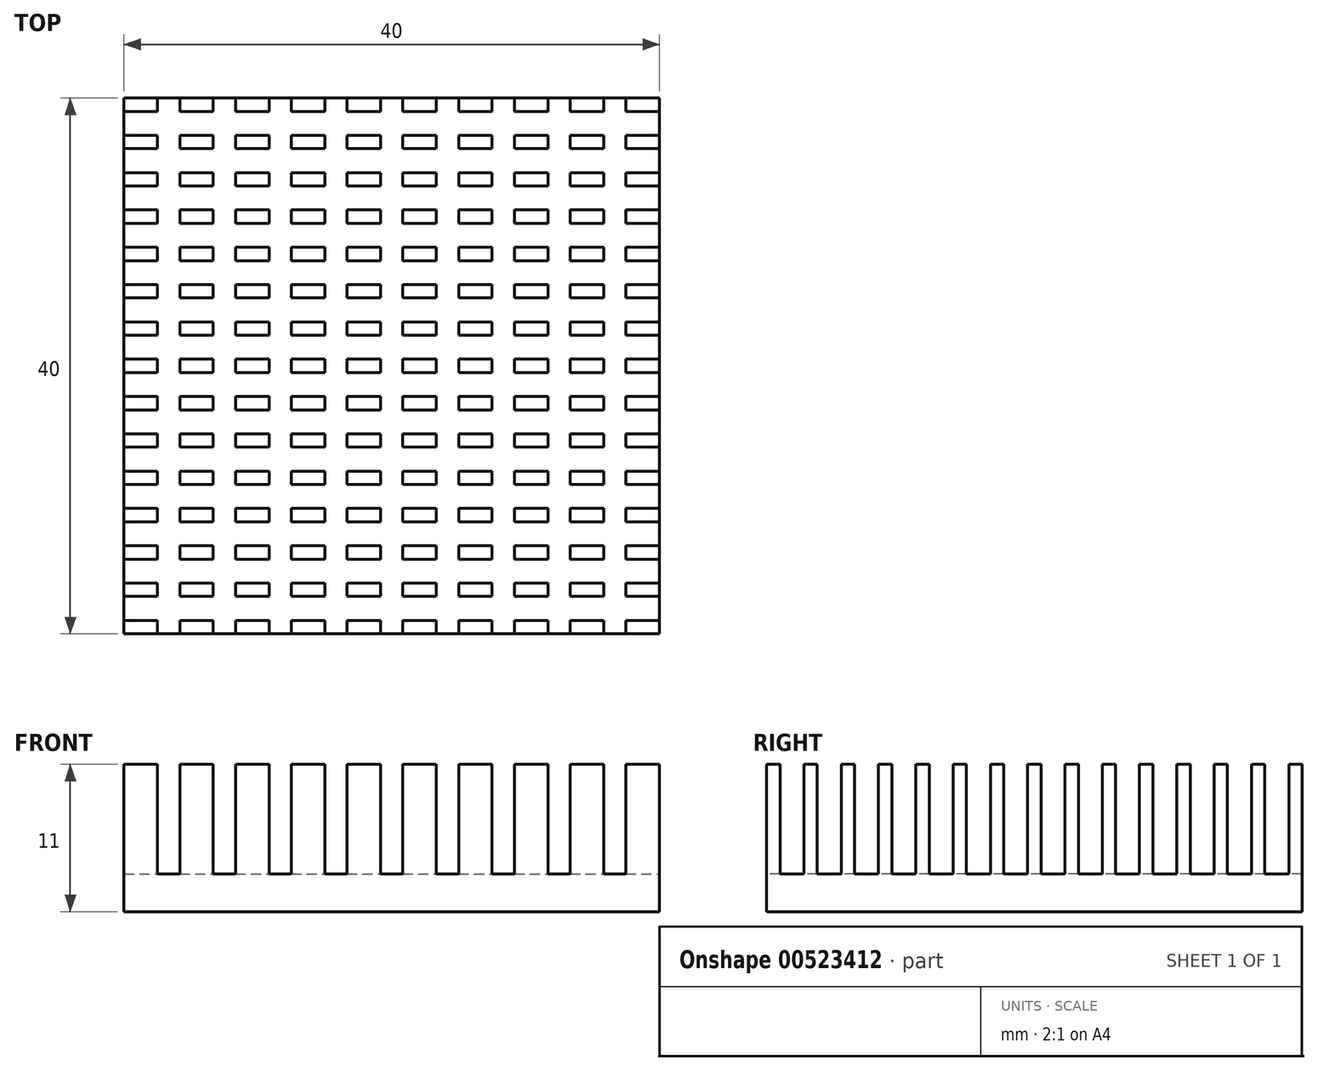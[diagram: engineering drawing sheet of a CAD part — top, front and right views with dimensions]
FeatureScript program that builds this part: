
annotation { "Feature Type Name" : "Feature", "Feature Type Description" : "" }
export const myFeature = defineFeature(function(context is Context, id is Id, definition is map)
    precondition{}
    {
        {
            var Q0;
            Q0=qCreatedBy(makeId("Top.planeOp"),FACE);
            var sketch = newSketch(context, id + "F0", { "sketchPlane" : qUnion([Q0])});
            skLineSegment(sketch, "E0.bottom", {"start": v(-20, 20) * mm, "end": v(20, 20) * mm});
            skLineSegment(sketch, "E0.top", {"start": v(-20, -20) * mm, "end": v(20, -20) * mm});
            skLineSegment(sketch, "E0.left", {"start": v(-20, 20) * mm, "end": v(-20, -20) * mm});
            skLineSegment(sketch, "E0.right", {"start": v(20, 20) * mm, "end": v(20, -20) * mm});
            skPoint(sketch, "E0.middle", {"position": v(0, 0) * mm});
            skSolve(sketch);
        }
        {
            var Q0;
            Q0 = qSketchRegion(id + "F0", true);
            extrude(context, id + "F1", {"entities" : qUnion([Q0]), "depth" : 2.8 * mm, "offsetDistance" : 25 * mm});
        }
        {
            var Q0;
            Q0=makeQuery(id+"F1.opExtrude","CAP_FACE",FACE,{"disambiguationData":[OSD([sQuery(id+"F0.wireOp",EDGE,"E0.bottom"),sQuery(id+"F0.wireOp",EDGE,"E0.top"),sQuery(id+"F0.wireOp",EDGE,"E0.left"),sQuery(id+"F0.wireOp",EDGE,"E0.right")])],"isStart":false});
            var sketch = newSketch(context, id + "F2", { "sketchPlane" : qUnion([Q0])});
            skLineSegment(sketch, "E1.bottom", {"start": v(-20, 20) * mm, "end": v(-17.5, 20) * mm});
            skLineSegment(sketch, "E1.top", {"start": v(-20, 19) * mm, "end": v(-17.5, 19) * mm});
            skLineSegment(sketch, "E1.left", {"start": v(-20, 20) * mm, "end": v(-20, 19) * mm});
            skLineSegment(sketch, "E1.right", {"start": v(-17.5, 20) * mm, "end": v(-17.5, 19) * mm});
            skPoint(sketch, "E1.middle", {"position": v(-18.75, 19.5) * mm});
            skLineSegment(sketch, "E2.1.0.0", {"start": v(-13.33, 20) * mm, "end": v(-13.33, 19) * mm});
            skLineSegment(sketch, "E2.1.0.1", {"start": v(-15.83, 20) * mm, "end": v(-15.83, 19) * mm});
            skLineSegment(sketch, "E2.1.0.2", {"start": v(-15.83, 19) * mm, "end": v(-13.33, 19) * mm});
            skLineSegment(sketch, "E2.1.0.3", {"start": v(-15.83, 20) * mm, "end": v(-13.33, 20) * mm});
            skPoint(sketch, "E2.1.0.4", {"position": v(-14.58, 19.5) * mm});
            skLineSegment(sketch, "E2.2.0.0", {"start": v(-9.17, 20) * mm, "end": v(-9.17, 19) * mm});
            skLineSegment(sketch, "E2.2.0.1", {"start": v(-11.67, 20) * mm, "end": v(-11.67, 19) * mm});
            skLineSegment(sketch, "E2.2.0.2", {"start": v(-11.67, 19) * mm, "end": v(-9.17, 19) * mm});
            skLineSegment(sketch, "E2.2.0.3", {"start": v(-11.67, 20) * mm, "end": v(-9.17, 20) * mm});
            skPoint(sketch, "E2.2.0.4", {"position": v(-10.42, 19.5) * mm});
            skLineSegment(sketch, "E2.3.0.0", {"start": v(-5, 20) * mm, "end": v(-5, 19) * mm});
            skLineSegment(sketch, "E2.3.0.1", {"start": v(-7.5, 20) * mm, "end": v(-7.5, 19) * mm});
            skLineSegment(sketch, "E2.3.0.2", {"start": v(-7.5, 19) * mm, "end": v(-5, 19) * mm});
            skLineSegment(sketch, "E2.3.0.3", {"start": v(-7.5, 20) * mm, "end": v(-5, 20) * mm});
            skPoint(sketch, "E2.3.0.4", {"position": v(-6.25, 19.5) * mm});
            skLineSegment(sketch, "E2.4.0.0", {"start": v(-0.83, 20) * mm, "end": v(-0.83, 19) * mm});
            skLineSegment(sketch, "E2.4.0.1", {"start": v(-3.33, 20) * mm, "end": v(-3.33, 19) * mm});
            skLineSegment(sketch, "E2.4.0.2", {"start": v(-3.33, 19) * mm, "end": v(-0.83, 19) * mm});
            skLineSegment(sketch, "E2.4.0.3", {"start": v(-3.33, 20) * mm, "end": v(-0.83, 20) * mm});
            skPoint(sketch, "E2.4.0.4", {"position": v(-2.08, 19.5) * mm});
            skLineSegment(sketch, "E2.5.0.0", {"start": v(3.33, 20) * mm, "end": v(3.33, 19) * mm});
            skLineSegment(sketch, "E2.5.0.1", {"start": v(0.83, 20) * mm, "end": v(0.83, 19) * mm});
            skLineSegment(sketch, "E2.5.0.2", {"start": v(0.83, 19) * mm, "end": v(3.33, 19) * mm});
            skLineSegment(sketch, "E2.5.0.3", {"start": v(0.83, 20) * mm, "end": v(3.33, 20) * mm});
            skPoint(sketch, "E2.5.0.4", {"position": v(2.08, 19.5) * mm});
            skLineSegment(sketch, "E2.6.0.0", {"start": v(7.5, 20) * mm, "end": v(7.5, 19) * mm});
            skLineSegment(sketch, "E2.6.0.1", {"start": v(5, 20) * mm, "end": v(5, 19) * mm});
            skLineSegment(sketch, "E2.6.0.2", {"start": v(5, 19) * mm, "end": v(7.5, 19) * mm});
            skLineSegment(sketch, "E2.6.0.3", {"start": v(5, 20) * mm, "end": v(7.5, 20) * mm});
            skPoint(sketch, "E2.6.0.4", {"position": v(6.25, 19.5) * mm});
            skLineSegment(sketch, "E2.7.0.0", {"start": v(11.67, 20) * mm, "end": v(11.67, 19) * mm});
            skLineSegment(sketch, "E2.7.0.1", {"start": v(9.17, 20) * mm, "end": v(9.17, 19) * mm});
            skLineSegment(sketch, "E2.7.0.2", {"start": v(9.17, 19) * mm, "end": v(11.67, 19) * mm});
            skLineSegment(sketch, "E2.7.0.3", {"start": v(9.17, 20) * mm, "end": v(11.67, 20) * mm});
            skPoint(sketch, "E2.7.0.4", {"position": v(10.42, 19.5) * mm});
            skLineSegment(sketch, "E2.8.0.0", {"start": v(15.83, 20) * mm, "end": v(15.83, 19) * mm});
            skLineSegment(sketch, "E2.8.0.1", {"start": v(13.33, 20) * mm, "end": v(13.33, 19) * mm});
            skLineSegment(sketch, "E2.8.0.2", {"start": v(13.33, 19) * mm, "end": v(15.83, 19) * mm});
            skLineSegment(sketch, "E2.8.0.3", {"start": v(13.33, 20) * mm, "end": v(15.83, 20) * mm});
            skPoint(sketch, "E2.8.0.4", {"position": v(14.58, 19.5) * mm});
            skLineSegment(sketch, "E2.9.0.0", {"start": v(20, 20) * mm, "end": v(20, 19) * mm});
            skLineSegment(sketch, "E2.9.0.1", {"start": v(17.5, 20) * mm, "end": v(17.5, 19) * mm});
            skLineSegment(sketch, "E2.9.0.2", {"start": v(17.5, 19) * mm, "end": v(20, 19) * mm});
            skLineSegment(sketch, "E2.9.0.3", {"start": v(17.5, 20) * mm, "end": v(20, 20) * mm});
            skPoint(sketch, "E2.9.0.4", {"position": v(18.75, 19.5) * mm});
            skLineSegment(sketch, "E2.direction1", {"start": v(-20, 19) * mm, "end": v(-15.83, 19) * mm, "construction": true});
            skPoint(sketch, "E3.1.0.0", {"position": v(2.08, 16.71) * mm});
            skLineSegment(sketch, "E3.1.0.1", {"start": v(5, 17.21) * mm, "end": v(7.5, 17.21) * mm});
            skLineSegment(sketch, "E3.1.0.2", {"start": v(17.5, 17.21) * mm, "end": v(20, 17.21) * mm});
            skLineSegment(sketch, "E3.1.0.3", {"start": v(0.83, 17.21) * mm, "end": v(3.33, 17.21) * mm});
            skPoint(sketch, "E3.1.0.4", {"position": v(18.75, 16.71) * mm});
            skPoint(sketch, "E3.1.0.5", {"position": v(-6.25, 16.71) * mm});
            skLineSegment(sketch, "E3.1.0.6", {"start": v(-20, 16.21) * mm, "end": v(-15.83, 16.21) * mm, "construction": true});
            skLineSegment(sketch, "E3.1.0.7", {"start": v(9.17, 16.21) * mm, "end": v(11.67, 16.21) * mm});
            skPoint(sketch, "E3.1.0.8", {"position": v(6.25, 16.71) * mm});
            skPoint(sketch, "E3.1.0.9", {"position": v(-2.08, 16.71) * mm});
            skLineSegment(sketch, "E3.1.0.10", {"start": v(-7.5, 16.21) * mm, "end": v(-5, 16.21) * mm});
            skPoint(sketch, "E3.1.0.11", {"position": v(-18.75, 16.71) * mm});
            skLineSegment(sketch, "E3.1.0.12", {"start": v(-7.5, 17.21) * mm, "end": v(-5, 17.21) * mm});
            skLineSegment(sketch, "E3.1.0.13", {"start": v(-20, 17.21) * mm, "end": v(-17.5, 17.21) * mm});
            skLineSegment(sketch, "E3.1.0.14", {"start": v(-15.83, 16.21) * mm, "end": v(-13.33, 16.21) * mm});
            skLineSegment(sketch, "E3.1.0.15", {"start": v(-15.83, 17.21) * mm, "end": v(-13.33, 17.21) * mm});
            skLineSegment(sketch, "E3.1.0.16", {"start": v(-11.67, 16.21) * mm, "end": v(-9.17, 16.21) * mm});
            skLineSegment(sketch, "E3.1.0.17", {"start": v(-11.67, 17.21) * mm, "end": v(-9.17, 17.21) * mm});
            skLineSegment(sketch, "E3.1.0.18", {"start": v(9.17, 17.21) * mm, "end": v(11.67, 17.21) * mm});
            skLineSegment(sketch, "E3.1.0.19", {"start": v(17.5, 16.21) * mm, "end": v(20, 16.21) * mm});
            skLineSegment(sketch, "E3.1.0.20", {"start": v(0.83, 16.21) * mm, "end": v(3.33, 16.21) * mm});
            skLineSegment(sketch, "E3.1.0.21", {"start": v(13.33, 16.21) * mm, "end": v(15.83, 16.21) * mm});
            skLineSegment(sketch, "E3.1.0.22", {"start": v(-3.33, 16.21) * mm, "end": v(-0.83, 16.21) * mm});
            skPoint(sketch, "E3.1.0.23", {"position": v(10.42, 16.71) * mm});
            skPoint(sketch, "E3.1.0.24", {"position": v(-14.58, 16.71) * mm});
            skLineSegment(sketch, "E3.1.0.25", {"start": v(5, 16.21) * mm, "end": v(7.5, 16.21) * mm});
            skLineSegment(sketch, "E3.1.0.26", {"start": v(13.33, 17.21) * mm, "end": v(15.83, 17.21) * mm});
            skLineSegment(sketch, "E3.1.0.27", {"start": v(-3.33, 17.21) * mm, "end": v(-0.83, 17.21) * mm});
            skPoint(sketch, "E3.1.0.28", {"position": v(14.58, 16.71) * mm});
            skPoint(sketch, "E3.1.0.29", {"position": v(-10.42, 16.71) * mm});
            skLineSegment(sketch, "E3.1.0.30", {"start": v(-20, 16.21) * mm, "end": v(-17.5, 16.21) * mm});
            skLineSegment(sketch, "E3.1.0.31", {"start": v(20, 17.21) * mm, "end": v(20, 16.21) * mm});
            skLineSegment(sketch, "E3.1.0.32", {"start": v(9.17, 17.21) * mm, "end": v(9.17, 16.21) * mm});
            skLineSegment(sketch, "E3.1.0.33", {"start": v(3.33, 17.21) * mm, "end": v(3.33, 16.21) * mm});
            skLineSegment(sketch, "E3.1.0.34", {"start": v(15.83, 17.21) * mm, "end": v(15.83, 16.21) * mm});
            skLineSegment(sketch, "E3.1.0.35", {"start": v(-0.83, 17.21) * mm, "end": v(-0.83, 16.21) * mm});
            skLineSegment(sketch, "E3.1.0.36", {"start": v(11.67, 17.21) * mm, "end": v(11.67, 16.21) * mm});
            skLineSegment(sketch, "E3.1.0.37", {"start": v(7.5, 17.21) * mm, "end": v(7.5, 16.21) * mm});
            skLineSegment(sketch, "E3.1.0.38", {"start": v(17.5, 17.21) * mm, "end": v(17.5, 16.21) * mm});
            skLineSegment(sketch, "E3.1.0.39", {"start": v(0.83, 17.21) * mm, "end": v(0.83, 16.21) * mm});
            skLineSegment(sketch, "E3.1.0.40", {"start": v(13.33, 17.21) * mm, "end": v(13.33, 16.21) * mm});
            skLineSegment(sketch, "E3.1.0.41", {"start": v(-3.33, 17.21) * mm, "end": v(-3.33, 16.21) * mm});
            skLineSegment(sketch, "E3.1.0.42", {"start": v(-7.5, 17.21) * mm, "end": v(-7.5, 16.21) * mm});
            skLineSegment(sketch, "E3.1.0.43", {"start": v(-20, 17.21) * mm, "end": v(-20, 16.21) * mm});
            skLineSegment(sketch, "E3.1.0.44", {"start": v(-17.5, 17.21) * mm, "end": v(-17.5, 16.21) * mm});
            skLineSegment(sketch, "E3.1.0.45", {"start": v(-13.33, 17.21) * mm, "end": v(-13.33, 16.21) * mm});
            skLineSegment(sketch, "E3.1.0.46", {"start": v(-15.83, 17.21) * mm, "end": v(-15.83, 16.21) * mm});
            skLineSegment(sketch, "E3.1.0.47", {"start": v(-9.17, 17.21) * mm, "end": v(-9.17, 16.21) * mm});
            skLineSegment(sketch, "E3.1.0.48", {"start": v(-11.67, 17.21) * mm, "end": v(-11.67, 16.21) * mm});
            skLineSegment(sketch, "E3.1.0.49", {"start": v(5, 17.21) * mm, "end": v(5, 16.21) * mm});
            skLineSegment(sketch, "E3.1.0.50", {"start": v(-5, 17.21) * mm, "end": v(-5, 16.21) * mm});
            skPoint(sketch, "E3.2.0.0", {"position": v(2.08, 13.93) * mm});
            skLineSegment(sketch, "E3.2.0.1", {"start": v(5, 14.43) * mm, "end": v(7.5, 14.43) * mm});
            skLineSegment(sketch, "E3.2.0.2", {"start": v(17.5, 14.43) * mm, "end": v(20, 14.43) * mm});
            skLineSegment(sketch, "E3.2.0.3", {"start": v(0.83, 14.43) * mm, "end": v(3.33, 14.43) * mm});
            skPoint(sketch, "E3.2.0.4", {"position": v(18.75, 13.93) * mm});
            skPoint(sketch, "E3.2.0.5", {"position": v(-6.25, 13.93) * mm});
            skLineSegment(sketch, "E3.2.0.6", {"start": v(-20, 13.43) * mm, "end": v(-15.83, 13.43) * mm, "construction": true});
            skLineSegment(sketch, "E3.2.0.7", {"start": v(9.17, 13.43) * mm, "end": v(11.67, 13.43) * mm});
            skPoint(sketch, "E3.2.0.8", {"position": v(6.25, 13.93) * mm});
            skPoint(sketch, "E3.2.0.9", {"position": v(-2.08, 13.93) * mm});
            skLineSegment(sketch, "E3.2.0.10", {"start": v(-7.5, 13.43) * mm, "end": v(-5, 13.43) * mm});
            skPoint(sketch, "E3.2.0.11", {"position": v(-18.75, 13.93) * mm});
            skLineSegment(sketch, "E3.2.0.12", {"start": v(-7.5, 14.43) * mm, "end": v(-5, 14.43) * mm});
            skLineSegment(sketch, "E3.2.0.13", {"start": v(-20, 14.43) * mm, "end": v(-17.5, 14.43) * mm});
            skLineSegment(sketch, "E3.2.0.14", {"start": v(-15.83, 13.43) * mm, "end": v(-13.33, 13.43) * mm});
            skLineSegment(sketch, "E3.2.0.15", {"start": v(-15.83, 14.43) * mm, "end": v(-13.33, 14.43) * mm});
            skLineSegment(sketch, "E3.2.0.16", {"start": v(-11.67, 13.43) * mm, "end": v(-9.17, 13.43) * mm});
            skLineSegment(sketch, "E3.2.0.17", {"start": v(-11.67, 14.43) * mm, "end": v(-9.17, 14.43) * mm});
            skLineSegment(sketch, "E3.2.0.18", {"start": v(9.17, 14.43) * mm, "end": v(11.67, 14.43) * mm});
            skLineSegment(sketch, "E3.2.0.19", {"start": v(17.5, 13.43) * mm, "end": v(20, 13.43) * mm});
            skLineSegment(sketch, "E3.2.0.20", {"start": v(0.83, 13.43) * mm, "end": v(3.33, 13.43) * mm});
            skLineSegment(sketch, "E3.2.0.21", {"start": v(13.33, 13.43) * mm, "end": v(15.83, 13.43) * mm});
            skLineSegment(sketch, "E3.2.0.22", {"start": v(-3.33, 13.43) * mm, "end": v(-0.83, 13.43) * mm});
            skPoint(sketch, "E3.2.0.23", {"position": v(10.42, 13.93) * mm});
            skPoint(sketch, "E3.2.0.24", {"position": v(-14.58, 13.93) * mm});
            skLineSegment(sketch, "E3.2.0.25", {"start": v(5, 13.43) * mm, "end": v(7.5, 13.43) * mm});
            skLineSegment(sketch, "E3.2.0.26", {"start": v(13.33, 14.43) * mm, "end": v(15.83, 14.43) * mm});
            skLineSegment(sketch, "E3.2.0.27", {"start": v(-3.33, 14.43) * mm, "end": v(-0.83, 14.43) * mm});
            skPoint(sketch, "E3.2.0.28", {"position": v(14.58, 13.93) * mm});
            skPoint(sketch, "E3.2.0.29", {"position": v(-10.42, 13.93) * mm});
            skLineSegment(sketch, "E3.2.0.30", {"start": v(-20, 13.43) * mm, "end": v(-17.5, 13.43) * mm});
            skLineSegment(sketch, "E3.2.0.31", {"start": v(20, 14.43) * mm, "end": v(20, 13.43) * mm});
            skLineSegment(sketch, "E3.2.0.32", {"start": v(9.17, 14.43) * mm, "end": v(9.17, 13.43) * mm});
            skLineSegment(sketch, "E3.2.0.33", {"start": v(3.33, 14.43) * mm, "end": v(3.33, 13.43) * mm});
            skLineSegment(sketch, "E3.2.0.34", {"start": v(15.83, 14.43) * mm, "end": v(15.83, 13.43) * mm});
            skLineSegment(sketch, "E3.2.0.35", {"start": v(-0.83, 14.43) * mm, "end": v(-0.83, 13.43) * mm});
            skLineSegment(sketch, "E3.2.0.36", {"start": v(11.67, 14.43) * mm, "end": v(11.67, 13.43) * mm});
            skLineSegment(sketch, "E3.2.0.37", {"start": v(7.5, 14.43) * mm, "end": v(7.5, 13.43) * mm});
            skLineSegment(sketch, "E3.2.0.38", {"start": v(17.5, 14.43) * mm, "end": v(17.5, 13.43) * mm});
            skLineSegment(sketch, "E3.2.0.39", {"start": v(0.83, 14.43) * mm, "end": v(0.83, 13.43) * mm});
            skLineSegment(sketch, "E3.2.0.40", {"start": v(13.33, 14.43) * mm, "end": v(13.33, 13.43) * mm});
            skLineSegment(sketch, "E3.2.0.41", {"start": v(-3.33, 14.43) * mm, "end": v(-3.33, 13.43) * mm});
            skLineSegment(sketch, "E3.2.0.42", {"start": v(-7.5, 14.43) * mm, "end": v(-7.5, 13.43) * mm});
            skLineSegment(sketch, "E3.2.0.43", {"start": v(-20, 14.43) * mm, "end": v(-20, 13.43) * mm});
            skLineSegment(sketch, "E3.2.0.44", {"start": v(-17.5, 14.43) * mm, "end": v(-17.5, 13.43) * mm});
            skLineSegment(sketch, "E3.2.0.45", {"start": v(-13.33, 14.43) * mm, "end": v(-13.33, 13.43) * mm});
            skLineSegment(sketch, "E3.2.0.46", {"start": v(-15.83, 14.43) * mm, "end": v(-15.83, 13.43) * mm});
            skLineSegment(sketch, "E3.2.0.47", {"start": v(-9.17, 14.43) * mm, "end": v(-9.17, 13.43) * mm});
            skLineSegment(sketch, "E3.2.0.48", {"start": v(-11.67, 14.43) * mm, "end": v(-11.67, 13.43) * mm});
            skLineSegment(sketch, "E3.2.0.49", {"start": v(5, 14.43) * mm, "end": v(5, 13.43) * mm});
            skLineSegment(sketch, "E3.2.0.50", {"start": v(-5, 14.43) * mm, "end": v(-5, 13.43) * mm});
            skPoint(sketch, "E3.3.0.0", {"position": v(2.08, 11.14) * mm});
            skLineSegment(sketch, "E3.3.0.1", {"start": v(5, 11.64) * mm, "end": v(7.5, 11.64) * mm});
            skLineSegment(sketch, "E3.3.0.2", {"start": v(17.5, 11.64) * mm, "end": v(20, 11.64) * mm});
            skLineSegment(sketch, "E3.3.0.3", {"start": v(0.83, 11.64) * mm, "end": v(3.33, 11.64) * mm});
            skPoint(sketch, "E3.3.0.4", {"position": v(18.75, 11.14) * mm});
            skPoint(sketch, "E3.3.0.5", {"position": v(-6.25, 11.14) * mm});
            skLineSegment(sketch, "E3.3.0.6", {"start": v(-20, 10.64) * mm, "end": v(-15.83, 10.64) * mm, "construction": true});
            skLineSegment(sketch, "E3.3.0.7", {"start": v(9.17, 10.64) * mm, "end": v(11.67, 10.64) * mm});
            skPoint(sketch, "E3.3.0.8", {"position": v(6.25, 11.14) * mm});
            skPoint(sketch, "E3.3.0.9", {"position": v(-2.08, 11.14) * mm});
            skLineSegment(sketch, "E3.3.0.10", {"start": v(-7.5, 10.64) * mm, "end": v(-5, 10.64) * mm});
            skPoint(sketch, "E3.3.0.11", {"position": v(-18.75, 11.14) * mm});
            skLineSegment(sketch, "E3.3.0.12", {"start": v(-7.5, 11.64) * mm, "end": v(-5, 11.64) * mm});
            skLineSegment(sketch, "E3.3.0.13", {"start": v(-20, 11.64) * mm, "end": v(-17.5, 11.64) * mm});
            skLineSegment(sketch, "E3.3.0.14", {"start": v(-15.83, 10.64) * mm, "end": v(-13.33, 10.64) * mm});
            skLineSegment(sketch, "E3.3.0.15", {"start": v(-15.83, 11.64) * mm, "end": v(-13.33, 11.64) * mm});
            skLineSegment(sketch, "E3.3.0.16", {"start": v(-11.67, 10.64) * mm, "end": v(-9.17, 10.64) * mm});
            skLineSegment(sketch, "E3.3.0.17", {"start": v(-11.67, 11.64) * mm, "end": v(-9.17, 11.64) * mm});
            skLineSegment(sketch, "E3.3.0.18", {"start": v(9.17, 11.64) * mm, "end": v(11.67, 11.64) * mm});
            skLineSegment(sketch, "E3.3.0.19", {"start": v(17.5, 10.64) * mm, "end": v(20, 10.64) * mm});
            skLineSegment(sketch, "E3.3.0.20", {"start": v(0.83, 10.64) * mm, "end": v(3.33, 10.64) * mm});
            skLineSegment(sketch, "E3.3.0.21", {"start": v(13.33, 10.64) * mm, "end": v(15.83, 10.64) * mm});
            skLineSegment(sketch, "E3.3.0.22", {"start": v(-3.33, 10.64) * mm, "end": v(-0.83, 10.64) * mm});
            skPoint(sketch, "E3.3.0.23", {"position": v(10.42, 11.14) * mm});
            skPoint(sketch, "E3.3.0.24", {"position": v(-14.58, 11.14) * mm});
            skLineSegment(sketch, "E3.3.0.25", {"start": v(5, 10.64) * mm, "end": v(7.5, 10.64) * mm});
            skLineSegment(sketch, "E3.3.0.26", {"start": v(13.33, 11.64) * mm, "end": v(15.83, 11.64) * mm});
            skLineSegment(sketch, "E3.3.0.27", {"start": v(-3.33, 11.64) * mm, "end": v(-0.83, 11.64) * mm});
            skPoint(sketch, "E3.3.0.28", {"position": v(14.58, 11.14) * mm});
            skPoint(sketch, "E3.3.0.29", {"position": v(-10.42, 11.14) * mm});
            skLineSegment(sketch, "E3.3.0.30", {"start": v(-20, 10.64) * mm, "end": v(-17.5, 10.64) * mm});
            skLineSegment(sketch, "E3.3.0.31", {"start": v(20, 11.64) * mm, "end": v(20, 10.64) * mm});
            skLineSegment(sketch, "E3.3.0.32", {"start": v(9.17, 11.64) * mm, "end": v(9.17, 10.64) * mm});
            skLineSegment(sketch, "E3.3.0.33", {"start": v(3.33, 11.64) * mm, "end": v(3.33, 10.64) * mm});
            skLineSegment(sketch, "E3.3.0.34", {"start": v(15.83, 11.64) * mm, "end": v(15.83, 10.64) * mm});
            skLineSegment(sketch, "E3.3.0.35", {"start": v(-0.83, 11.64) * mm, "end": v(-0.83, 10.64) * mm});
            skLineSegment(sketch, "E3.3.0.36", {"start": v(11.67, 11.64) * mm, "end": v(11.67, 10.64) * mm});
            skLineSegment(sketch, "E3.3.0.37", {"start": v(7.5, 11.64) * mm, "end": v(7.5, 10.64) * mm});
            skLineSegment(sketch, "E3.3.0.38", {"start": v(17.5, 11.64) * mm, "end": v(17.5, 10.64) * mm});
            skLineSegment(sketch, "E3.3.0.39", {"start": v(0.83, 11.64) * mm, "end": v(0.83, 10.64) * mm});
            skLineSegment(sketch, "E3.3.0.40", {"start": v(13.33, 11.64) * mm, "end": v(13.33, 10.64) * mm});
            skLineSegment(sketch, "E3.3.0.41", {"start": v(-3.33, 11.64) * mm, "end": v(-3.33, 10.64) * mm});
            skLineSegment(sketch, "E3.3.0.42", {"start": v(-7.5, 11.64) * mm, "end": v(-7.5, 10.64) * mm});
            skLineSegment(sketch, "E3.3.0.43", {"start": v(-20, 11.64) * mm, "end": v(-20, 10.64) * mm});
            skLineSegment(sketch, "E3.3.0.44", {"start": v(-17.5, 11.64) * mm, "end": v(-17.5, 10.64) * mm});
            skLineSegment(sketch, "E3.3.0.45", {"start": v(-13.33, 11.64) * mm, "end": v(-13.33, 10.64) * mm});
            skLineSegment(sketch, "E3.3.0.46", {"start": v(-15.83, 11.64) * mm, "end": v(-15.83, 10.64) * mm});
            skLineSegment(sketch, "E3.3.0.47", {"start": v(-9.17, 11.64) * mm, "end": v(-9.17, 10.64) * mm});
            skLineSegment(sketch, "E3.3.0.48", {"start": v(-11.67, 11.64) * mm, "end": v(-11.67, 10.64) * mm});
            skLineSegment(sketch, "E3.3.0.49", {"start": v(5, 11.64) * mm, "end": v(5, 10.64) * mm});
            skLineSegment(sketch, "E3.3.0.50", {"start": v(-5, 11.64) * mm, "end": v(-5, 10.64) * mm});
            skPoint(sketch, "E3.4.0.0", {"position": v(2.08, 8.36) * mm});
            skLineSegment(sketch, "E3.4.0.1", {"start": v(5, 8.86) * mm, "end": v(7.5, 8.86) * mm});
            skLineSegment(sketch, "E3.4.0.2", {"start": v(17.5, 8.86) * mm, "end": v(20, 8.86) * mm});
            skLineSegment(sketch, "E3.4.0.3", {"start": v(0.83, 8.86) * mm, "end": v(3.33, 8.86) * mm});
            skPoint(sketch, "E3.4.0.4", {"position": v(18.75, 8.36) * mm});
            skPoint(sketch, "E3.4.0.5", {"position": v(-6.25, 8.36) * mm});
            skLineSegment(sketch, "E3.4.0.6", {"start": v(-20, 7.86) * mm, "end": v(-15.83, 7.86) * mm, "construction": true});
            skLineSegment(sketch, "E3.4.0.7", {"start": v(9.17, 7.86) * mm, "end": v(11.67, 7.86) * mm});
            skPoint(sketch, "E3.4.0.8", {"position": v(6.25, 8.36) * mm});
            skPoint(sketch, "E3.4.0.9", {"position": v(-2.08, 8.36) * mm});
            skLineSegment(sketch, "E3.4.0.10", {"start": v(-7.5, 7.86) * mm, "end": v(-5, 7.86) * mm});
            skPoint(sketch, "E3.4.0.11", {"position": v(-18.75, 8.36) * mm});
            skLineSegment(sketch, "E3.4.0.12", {"start": v(-7.5, 8.86) * mm, "end": v(-5, 8.86) * mm});
            skLineSegment(sketch, "E3.4.0.13", {"start": v(-20, 8.86) * mm, "end": v(-17.5, 8.86) * mm});
            skLineSegment(sketch, "E3.4.0.14", {"start": v(-15.83, 7.86) * mm, "end": v(-13.33, 7.86) * mm});
            skLineSegment(sketch, "E3.4.0.15", {"start": v(-15.83, 8.86) * mm, "end": v(-13.33, 8.86) * mm});
            skLineSegment(sketch, "E3.4.0.16", {"start": v(-11.67, 7.86) * mm, "end": v(-9.17, 7.86) * mm});
            skLineSegment(sketch, "E3.4.0.17", {"start": v(-11.67, 8.86) * mm, "end": v(-9.17, 8.86) * mm});
            skLineSegment(sketch, "E3.4.0.18", {"start": v(9.17, 8.86) * mm, "end": v(11.67, 8.86) * mm});
            skLineSegment(sketch, "E3.4.0.19", {"start": v(17.5, 7.86) * mm, "end": v(20, 7.86) * mm});
            skLineSegment(sketch, "E3.4.0.20", {"start": v(0.83, 7.86) * mm, "end": v(3.33, 7.86) * mm});
            skLineSegment(sketch, "E3.4.0.21", {"start": v(13.33, 7.86) * mm, "end": v(15.83, 7.86) * mm});
            skLineSegment(sketch, "E3.4.0.22", {"start": v(-3.33, 7.86) * mm, "end": v(-0.83, 7.86) * mm});
            skPoint(sketch, "E3.4.0.23", {"position": v(10.42, 8.36) * mm});
            skPoint(sketch, "E3.4.0.24", {"position": v(-14.58, 8.36) * mm});
            skLineSegment(sketch, "E3.4.0.25", {"start": v(5, 7.86) * mm, "end": v(7.5, 7.86) * mm});
            skLineSegment(sketch, "E3.4.0.26", {"start": v(13.33, 8.86) * mm, "end": v(15.83, 8.86) * mm});
            skLineSegment(sketch, "E3.4.0.27", {"start": v(-3.33, 8.86) * mm, "end": v(-0.83, 8.86) * mm});
            skPoint(sketch, "E3.4.0.28", {"position": v(14.58, 8.36) * mm});
            skPoint(sketch, "E3.4.0.29", {"position": v(-10.42, 8.36) * mm});
            skLineSegment(sketch, "E3.4.0.30", {"start": v(-20, 7.86) * mm, "end": v(-17.5, 7.86) * mm});
            skLineSegment(sketch, "E3.4.0.31", {"start": v(20, 8.86) * mm, "end": v(20, 7.86) * mm});
            skLineSegment(sketch, "E3.4.0.32", {"start": v(9.17, 8.86) * mm, "end": v(9.17, 7.86) * mm});
            skLineSegment(sketch, "E3.4.0.33", {"start": v(3.33, 8.86) * mm, "end": v(3.33, 7.86) * mm});
            skLineSegment(sketch, "E3.4.0.34", {"start": v(15.83, 8.86) * mm, "end": v(15.83, 7.86) * mm});
            skLineSegment(sketch, "E3.4.0.35", {"start": v(-0.83, 8.86) * mm, "end": v(-0.83, 7.86) * mm});
            skLineSegment(sketch, "E3.4.0.36", {"start": v(11.67, 8.86) * mm, "end": v(11.67, 7.86) * mm});
            skLineSegment(sketch, "E3.4.0.37", {"start": v(7.5, 8.86) * mm, "end": v(7.5, 7.86) * mm});
            skLineSegment(sketch, "E3.4.0.38", {"start": v(17.5, 8.86) * mm, "end": v(17.5, 7.86) * mm});
            skLineSegment(sketch, "E3.4.0.39", {"start": v(0.83, 8.86) * mm, "end": v(0.83, 7.86) * mm});
            skLineSegment(sketch, "E3.4.0.40", {"start": v(13.33, 8.86) * mm, "end": v(13.33, 7.86) * mm});
            skLineSegment(sketch, "E3.4.0.41", {"start": v(-3.33, 8.86) * mm, "end": v(-3.33, 7.86) * mm});
            skLineSegment(sketch, "E3.4.0.42", {"start": v(-7.5, 8.86) * mm, "end": v(-7.5, 7.86) * mm});
            skLineSegment(sketch, "E3.4.0.43", {"start": v(-20, 8.86) * mm, "end": v(-20, 7.86) * mm});
            skLineSegment(sketch, "E3.4.0.44", {"start": v(-17.5, 8.86) * mm, "end": v(-17.5, 7.86) * mm});
            skLineSegment(sketch, "E3.4.0.45", {"start": v(-13.33, 8.86) * mm, "end": v(-13.33, 7.86) * mm});
            skLineSegment(sketch, "E3.4.0.46", {"start": v(-15.83, 8.86) * mm, "end": v(-15.83, 7.86) * mm});
            skLineSegment(sketch, "E3.4.0.47", {"start": v(-9.17, 8.86) * mm, "end": v(-9.17, 7.86) * mm});
            skLineSegment(sketch, "E3.4.0.48", {"start": v(-11.67, 8.86) * mm, "end": v(-11.67, 7.86) * mm});
            skLineSegment(sketch, "E3.4.0.49", {"start": v(5, 8.86) * mm, "end": v(5, 7.86) * mm});
            skLineSegment(sketch, "E3.4.0.50", {"start": v(-5, 8.86) * mm, "end": v(-5, 7.86) * mm});
            skPoint(sketch, "E3.5.0.0", {"position": v(2.08, 5.57) * mm});
            skLineSegment(sketch, "E3.5.0.1", {"start": v(5, 6.07) * mm, "end": v(7.5, 6.07) * mm});
            skLineSegment(sketch, "E3.5.0.2", {"start": v(17.5, 6.07) * mm, "end": v(20, 6.07) * mm});
            skLineSegment(sketch, "E3.5.0.3", {"start": v(0.83, 6.07) * mm, "end": v(3.33, 6.07) * mm});
            skPoint(sketch, "E3.5.0.4", {"position": v(18.75, 5.57) * mm});
            skPoint(sketch, "E3.5.0.5", {"position": v(-6.25, 5.57) * mm});
            skLineSegment(sketch, "E3.5.0.6", {"start": v(-20, 5.07) * mm, "end": v(-15.83, 5.07) * mm, "construction": true});
            skLineSegment(sketch, "E3.5.0.7", {"start": v(9.17, 5.07) * mm, "end": v(11.67, 5.07) * mm});
            skPoint(sketch, "E3.5.0.8", {"position": v(6.25, 5.57) * mm});
            skPoint(sketch, "E3.5.0.9", {"position": v(-2.08, 5.57) * mm});
            skLineSegment(sketch, "E3.5.0.10", {"start": v(-7.5, 5.07) * mm, "end": v(-5, 5.07) * mm});
            skPoint(sketch, "E3.5.0.11", {"position": v(-18.75, 5.57) * mm});
            skLineSegment(sketch, "E3.5.0.12", {"start": v(-7.5, 6.07) * mm, "end": v(-5, 6.07) * mm});
            skLineSegment(sketch, "E3.5.0.13", {"start": v(-20, 6.07) * mm, "end": v(-17.5, 6.07) * mm});
            skLineSegment(sketch, "E3.5.0.14", {"start": v(-15.83, 5.07) * mm, "end": v(-13.33, 5.07) * mm});
            skLineSegment(sketch, "E3.5.0.15", {"start": v(-15.83, 6.07) * mm, "end": v(-13.33, 6.07) * mm});
            skLineSegment(sketch, "E3.5.0.16", {"start": v(-11.67, 5.07) * mm, "end": v(-9.17, 5.07) * mm});
            skLineSegment(sketch, "E3.5.0.17", {"start": v(-11.67, 6.07) * mm, "end": v(-9.17, 6.07) * mm});
            skLineSegment(sketch, "E3.5.0.18", {"start": v(9.17, 6.07) * mm, "end": v(11.67, 6.07) * mm});
            skLineSegment(sketch, "E3.5.0.19", {"start": v(17.5, 5.07) * mm, "end": v(20, 5.07) * mm});
            skLineSegment(sketch, "E3.5.0.20", {"start": v(0.83, 5.07) * mm, "end": v(3.33, 5.07) * mm});
            skLineSegment(sketch, "E3.5.0.21", {"start": v(13.33, 5.07) * mm, "end": v(15.83, 5.07) * mm});
            skLineSegment(sketch, "E3.5.0.22", {"start": v(-3.33, 5.07) * mm, "end": v(-0.83, 5.07) * mm});
            skPoint(sketch, "E3.5.0.23", {"position": v(10.42, 5.57) * mm});
            skPoint(sketch, "E3.5.0.24", {"position": v(-14.58, 5.57) * mm});
            skLineSegment(sketch, "E3.5.0.25", {"start": v(5, 5.07) * mm, "end": v(7.5, 5.07) * mm});
            skLineSegment(sketch, "E3.5.0.26", {"start": v(13.33, 6.07) * mm, "end": v(15.83, 6.07) * mm});
            skLineSegment(sketch, "E3.5.0.27", {"start": v(-3.33, 6.07) * mm, "end": v(-0.83, 6.07) * mm});
            skPoint(sketch, "E3.5.0.28", {"position": v(14.58, 5.57) * mm});
            skPoint(sketch, "E3.5.0.29", {"position": v(-10.42, 5.57) * mm});
            skLineSegment(sketch, "E3.5.0.30", {"start": v(-20, 5.07) * mm, "end": v(-17.5, 5.07) * mm});
            skLineSegment(sketch, "E3.5.0.31", {"start": v(20, 6.07) * mm, "end": v(20, 5.07) * mm});
            skLineSegment(sketch, "E3.5.0.32", {"start": v(9.17, 6.07) * mm, "end": v(9.17, 5.07) * mm});
            skLineSegment(sketch, "E3.5.0.33", {"start": v(3.33, 6.07) * mm, "end": v(3.33, 5.07) * mm});
            skLineSegment(sketch, "E3.5.0.34", {"start": v(15.83, 6.07) * mm, "end": v(15.83, 5.07) * mm});
            skLineSegment(sketch, "E3.5.0.35", {"start": v(-0.83, 6.07) * mm, "end": v(-0.83, 5.07) * mm});
            skLineSegment(sketch, "E3.5.0.36", {"start": v(11.67, 6.07) * mm, "end": v(11.67, 5.07) * mm});
            skLineSegment(sketch, "E3.5.0.37", {"start": v(7.5, 6.07) * mm, "end": v(7.5, 5.07) * mm});
            skLineSegment(sketch, "E3.5.0.38", {"start": v(17.5, 6.07) * mm, "end": v(17.5, 5.07) * mm});
            skLineSegment(sketch, "E3.5.0.39", {"start": v(0.83, 6.07) * mm, "end": v(0.83, 5.07) * mm});
            skLineSegment(sketch, "E3.5.0.40", {"start": v(13.33, 6.07) * mm, "end": v(13.33, 5.07) * mm});
            skLineSegment(sketch, "E3.5.0.41", {"start": v(-3.33, 6.07) * mm, "end": v(-3.33, 5.07) * mm});
            skLineSegment(sketch, "E3.5.0.42", {"start": v(-7.5, 6.07) * mm, "end": v(-7.5, 5.07) * mm});
            skLineSegment(sketch, "E3.5.0.43", {"start": v(-20, 6.07) * mm, "end": v(-20, 5.07) * mm});
            skLineSegment(sketch, "E3.5.0.44", {"start": v(-17.5, 6.07) * mm, "end": v(-17.5, 5.07) * mm});
            skLineSegment(sketch, "E3.5.0.45", {"start": v(-13.33, 6.07) * mm, "end": v(-13.33, 5.07) * mm});
            skLineSegment(sketch, "E3.5.0.46", {"start": v(-15.83, 6.07) * mm, "end": v(-15.83, 5.07) * mm});
            skLineSegment(sketch, "E3.5.0.47", {"start": v(-9.17, 6.07) * mm, "end": v(-9.17, 5.07) * mm});
            skLineSegment(sketch, "E3.5.0.48", {"start": v(-11.67, 6.07) * mm, "end": v(-11.67, 5.07) * mm});
            skLineSegment(sketch, "E3.5.0.49", {"start": v(5, 6.07) * mm, "end": v(5, 5.07) * mm});
            skLineSegment(sketch, "E3.5.0.50", {"start": v(-5, 6.07) * mm, "end": v(-5, 5.07) * mm});
            skPoint(sketch, "E3.6.0.0", {"position": v(2.08, 2.79) * mm});
            skLineSegment(sketch, "E3.6.0.1", {"start": v(5, 3.29) * mm, "end": v(7.5, 3.29) * mm});
            skLineSegment(sketch, "E3.6.0.2", {"start": v(17.5, 3.29) * mm, "end": v(20, 3.29) * mm});
            skLineSegment(sketch, "E3.6.0.3", {"start": v(0.83, 3.29) * mm, "end": v(3.33, 3.29) * mm});
            skPoint(sketch, "E3.6.0.4", {"position": v(18.75, 2.79) * mm});
            skPoint(sketch, "E3.6.0.5", {"position": v(-6.25, 2.79) * mm});
            skLineSegment(sketch, "E3.6.0.6", {"start": v(-20, 2.29) * mm, "end": v(-15.83, 2.29) * mm, "construction": true});
            skLineSegment(sketch, "E3.6.0.7", {"start": v(9.17, 2.29) * mm, "end": v(11.67, 2.29) * mm});
            skPoint(sketch, "E3.6.0.8", {"position": v(6.25, 2.79) * mm});
            skPoint(sketch, "E3.6.0.9", {"position": v(-2.08, 2.79) * mm});
            skLineSegment(sketch, "E3.6.0.10", {"start": v(-7.5, 2.29) * mm, "end": v(-5, 2.29) * mm});
            skPoint(sketch, "E3.6.0.11", {"position": v(-18.75, 2.79) * mm});
            skLineSegment(sketch, "E3.6.0.12", {"start": v(-7.5, 3.29) * mm, "end": v(-5, 3.29) * mm});
            skLineSegment(sketch, "E3.6.0.13", {"start": v(-20, 3.29) * mm, "end": v(-17.5, 3.29) * mm});
            skLineSegment(sketch, "E3.6.0.14", {"start": v(-15.83, 2.29) * mm, "end": v(-13.33, 2.29) * mm});
            skLineSegment(sketch, "E3.6.0.15", {"start": v(-15.83, 3.29) * mm, "end": v(-13.33, 3.29) * mm});
            skLineSegment(sketch, "E3.6.0.16", {"start": v(-11.67, 2.29) * mm, "end": v(-9.17, 2.29) * mm});
            skLineSegment(sketch, "E3.6.0.17", {"start": v(-11.67, 3.29) * mm, "end": v(-9.17, 3.29) * mm});
            skLineSegment(sketch, "E3.6.0.18", {"start": v(9.17, 3.29) * mm, "end": v(11.67, 3.29) * mm});
            skLineSegment(sketch, "E3.6.0.19", {"start": v(17.5, 2.29) * mm, "end": v(20, 2.29) * mm});
            skLineSegment(sketch, "E3.6.0.20", {"start": v(0.83, 2.29) * mm, "end": v(3.33, 2.29) * mm});
            skLineSegment(sketch, "E3.6.0.21", {"start": v(13.33, 2.29) * mm, "end": v(15.83, 2.29) * mm});
            skLineSegment(sketch, "E3.6.0.22", {"start": v(-3.33, 2.29) * mm, "end": v(-0.83, 2.29) * mm});
            skPoint(sketch, "E3.6.0.23", {"position": v(10.42, 2.79) * mm});
            skPoint(sketch, "E3.6.0.24", {"position": v(-14.58, 2.79) * mm});
            skLineSegment(sketch, "E3.6.0.25", {"start": v(5, 2.29) * mm, "end": v(7.5, 2.29) * mm});
            skLineSegment(sketch, "E3.6.0.26", {"start": v(13.33, 3.29) * mm, "end": v(15.83, 3.29) * mm});
            skLineSegment(sketch, "E3.6.0.27", {"start": v(-3.33, 3.29) * mm, "end": v(-0.83, 3.29) * mm});
            skPoint(sketch, "E3.6.0.28", {"position": v(14.58, 2.79) * mm});
            skPoint(sketch, "E3.6.0.29", {"position": v(-10.42, 2.79) * mm});
            skLineSegment(sketch, "E3.6.0.30", {"start": v(-20, 2.29) * mm, "end": v(-17.5, 2.29) * mm});
            skLineSegment(sketch, "E3.6.0.31", {"start": v(20, 3.29) * mm, "end": v(20, 2.29) * mm});
            skLineSegment(sketch, "E3.6.0.32", {"start": v(9.17, 3.29) * mm, "end": v(9.17, 2.29) * mm});
            skLineSegment(sketch, "E3.6.0.33", {"start": v(3.33, 3.29) * mm, "end": v(3.33, 2.29) * mm});
            skLineSegment(sketch, "E3.6.0.34", {"start": v(15.83, 3.29) * mm, "end": v(15.83, 2.29) * mm});
            skLineSegment(sketch, "E3.6.0.35", {"start": v(-0.83, 3.29) * mm, "end": v(-0.83, 2.29) * mm});
            skLineSegment(sketch, "E3.6.0.36", {"start": v(11.67, 3.29) * mm, "end": v(11.67, 2.29) * mm});
            skLineSegment(sketch, "E3.6.0.37", {"start": v(7.5, 3.29) * mm, "end": v(7.5, 2.29) * mm});
            skLineSegment(sketch, "E3.6.0.38", {"start": v(17.5, 3.29) * mm, "end": v(17.5, 2.29) * mm});
            skLineSegment(sketch, "E3.6.0.39", {"start": v(0.83, 3.29) * mm, "end": v(0.83, 2.29) * mm});
            skLineSegment(sketch, "E3.6.0.40", {"start": v(13.33, 3.29) * mm, "end": v(13.33, 2.29) * mm});
            skLineSegment(sketch, "E3.6.0.41", {"start": v(-3.33, 3.29) * mm, "end": v(-3.33, 2.29) * mm});
            skLineSegment(sketch, "E3.6.0.42", {"start": v(-7.5, 3.29) * mm, "end": v(-7.5, 2.29) * mm});
            skLineSegment(sketch, "E3.6.0.43", {"start": v(-20, 3.29) * mm, "end": v(-20, 2.29) * mm});
            skLineSegment(sketch, "E3.6.0.44", {"start": v(-17.5, 3.29) * mm, "end": v(-17.5, 2.29) * mm});
            skLineSegment(sketch, "E3.6.0.45", {"start": v(-13.33, 3.29) * mm, "end": v(-13.33, 2.29) * mm});
            skLineSegment(sketch, "E3.6.0.46", {"start": v(-15.83, 3.29) * mm, "end": v(-15.83, 2.29) * mm});
            skLineSegment(sketch, "E3.6.0.47", {"start": v(-9.17, 3.29) * mm, "end": v(-9.17, 2.29) * mm});
            skLineSegment(sketch, "E3.6.0.48", {"start": v(-11.67, 3.29) * mm, "end": v(-11.67, 2.29) * mm});
            skLineSegment(sketch, "E3.6.0.49", {"start": v(5, 3.29) * mm, "end": v(5, 2.29) * mm});
            skLineSegment(sketch, "E3.6.0.50", {"start": v(-5, 3.29) * mm, "end": v(-5, 2.29) * mm});
            skPoint(sketch, "E3.7.0.0", {"position": v(2.08, 0) * mm});
            skLineSegment(sketch, "E3.7.0.1", {"start": v(5, 0.5) * mm, "end": v(7.5, 0.5) * mm});
            skLineSegment(sketch, "E3.7.0.2", {"start": v(17.5, 0.5) * mm, "end": v(20, 0.5) * mm});
            skLineSegment(sketch, "E3.7.0.3", {"start": v(0.83, 0.5) * mm, "end": v(3.33, 0.5) * mm});
            skPoint(sketch, "E3.7.0.4", {"position": v(18.75, 0) * mm});
            skPoint(sketch, "E3.7.0.5", {"position": v(-6.25, 0) * mm});
            skLineSegment(sketch, "E3.7.0.6", {"start": v(-20, -0.5) * mm, "end": v(-15.83, -0.5) * mm, "construction": true});
            skLineSegment(sketch, "E3.7.0.7", {"start": v(9.17, -0.5) * mm, "end": v(11.67, -0.5) * mm});
            skPoint(sketch, "E3.7.0.8", {"position": v(6.25, 0) * mm});
            skPoint(sketch, "E3.7.0.9", {"position": v(-2.08, 0) * mm});
            skLineSegment(sketch, "E3.7.0.10", {"start": v(-7.5, -0.5) * mm, "end": v(-5, -0.5) * mm});
            skPoint(sketch, "E3.7.0.11", {"position": v(-18.75, 0) * mm});
            skLineSegment(sketch, "E3.7.0.12", {"start": v(-7.5, 0.5) * mm, "end": v(-5, 0.5) * mm});
            skLineSegment(sketch, "E3.7.0.13", {"start": v(-20, 0.5) * mm, "end": v(-17.5, 0.5) * mm});
            skLineSegment(sketch, "E3.7.0.14", {"start": v(-15.83, -0.5) * mm, "end": v(-13.33, -0.5) * mm});
            skLineSegment(sketch, "E3.7.0.15", {"start": v(-15.83, 0.5) * mm, "end": v(-13.33, 0.5) * mm});
            skLineSegment(sketch, "E3.7.0.16", {"start": v(-11.67, -0.5) * mm, "end": v(-9.17, -0.5) * mm});
            skLineSegment(sketch, "E3.7.0.17", {"start": v(-11.67, 0.5) * mm, "end": v(-9.17, 0.5) * mm});
            skLineSegment(sketch, "E3.7.0.18", {"start": v(9.17, 0.5) * mm, "end": v(11.67, 0.5) * mm});
            skLineSegment(sketch, "E3.7.0.19", {"start": v(17.5, -0.5) * mm, "end": v(20, -0.5) * mm});
            skLineSegment(sketch, "E3.7.0.20", {"start": v(0.83, -0.5) * mm, "end": v(3.33, -0.5) * mm});
            skLineSegment(sketch, "E3.7.0.21", {"start": v(13.33, -0.5) * mm, "end": v(15.83, -0.5) * mm});
            skLineSegment(sketch, "E3.7.0.22", {"start": v(-3.33, -0.5) * mm, "end": v(-0.83, -0.5) * mm});
            skPoint(sketch, "E3.7.0.23", {"position": v(10.42, 0) * mm});
            skPoint(sketch, "E3.7.0.24", {"position": v(-14.58, 0) * mm});
            skLineSegment(sketch, "E3.7.0.25", {"start": v(5, -0.5) * mm, "end": v(7.5, -0.5) * mm});
            skLineSegment(sketch, "E3.7.0.26", {"start": v(13.33, 0.5) * mm, "end": v(15.83, 0.5) * mm});
            skLineSegment(sketch, "E3.7.0.27", {"start": v(-3.33, 0.5) * mm, "end": v(-0.83, 0.5) * mm});
            skPoint(sketch, "E3.7.0.28", {"position": v(14.58, 0) * mm});
            skPoint(sketch, "E3.7.0.29", {"position": v(-10.42, 0) * mm});
            skLineSegment(sketch, "E3.7.0.30", {"start": v(-20, -0.5) * mm, "end": v(-17.5, -0.5) * mm});
            skLineSegment(sketch, "E3.7.0.31", {"start": v(20, 0.5) * mm, "end": v(20, -0.5) * mm});
            skLineSegment(sketch, "E3.7.0.32", {"start": v(9.17, 0.5) * mm, "end": v(9.17, -0.5) * mm});
            skLineSegment(sketch, "E3.7.0.33", {"start": v(3.33, 0.5) * mm, "end": v(3.33, -0.5) * mm});
            skLineSegment(sketch, "E3.7.0.34", {"start": v(15.83, 0.5) * mm, "end": v(15.83, -0.5) * mm});
            skLineSegment(sketch, "E3.7.0.35", {"start": v(-0.83, 0.5) * mm, "end": v(-0.83, -0.5) * mm});
            skLineSegment(sketch, "E3.7.0.36", {"start": v(11.67, 0.5) * mm, "end": v(11.67, -0.5) * mm});
            skLineSegment(sketch, "E3.7.0.37", {"start": v(7.5, 0.5) * mm, "end": v(7.5, -0.5) * mm});
            skLineSegment(sketch, "E3.7.0.38", {"start": v(17.5, 0.5) * mm, "end": v(17.5, -0.5) * mm});
            skLineSegment(sketch, "E3.7.0.39", {"start": v(0.83, 0.5) * mm, "end": v(0.83, -0.5) * mm});
            skLineSegment(sketch, "E3.7.0.40", {"start": v(13.33, 0.5) * mm, "end": v(13.33, -0.5) * mm});
            skLineSegment(sketch, "E3.7.0.41", {"start": v(-3.33, 0.5) * mm, "end": v(-3.33, -0.5) * mm});
            skLineSegment(sketch, "E3.7.0.42", {"start": v(-7.5, 0.5) * mm, "end": v(-7.5, -0.5) * mm});
            skLineSegment(sketch, "E3.7.0.43", {"start": v(-20, 0.5) * mm, "end": v(-20, -0.5) * mm});
            skLineSegment(sketch, "E3.7.0.44", {"start": v(-17.5, 0.5) * mm, "end": v(-17.5, -0.5) * mm});
            skLineSegment(sketch, "E3.7.0.45", {"start": v(-13.33, 0.5) * mm, "end": v(-13.33, -0.5) * mm});
            skLineSegment(sketch, "E3.7.0.46", {"start": v(-15.83, 0.5) * mm, "end": v(-15.83, -0.5) * mm});
            skLineSegment(sketch, "E3.7.0.47", {"start": v(-9.17, 0.5) * mm, "end": v(-9.17, -0.5) * mm});
            skLineSegment(sketch, "E3.7.0.48", {"start": v(-11.67, 0.5) * mm, "end": v(-11.67, -0.5) * mm});
            skLineSegment(sketch, "E3.7.0.49", {"start": v(5, 0.5) * mm, "end": v(5, -0.5) * mm});
            skLineSegment(sketch, "E3.7.0.50", {"start": v(-5, 0.5) * mm, "end": v(-5, -0.5) * mm});
            skPoint(sketch, "E3.8.0.0", {"position": v(2.08, -2.79) * mm});
            skLineSegment(sketch, "E3.8.0.1", {"start": v(5, -2.29) * mm, "end": v(7.5, -2.29) * mm});
            skLineSegment(sketch, "E3.8.0.2", {"start": v(17.5, -2.29) * mm, "end": v(20, -2.29) * mm});
            skLineSegment(sketch, "E3.8.0.3", {"start": v(0.83, -2.29) * mm, "end": v(3.33, -2.29) * mm});
            skPoint(sketch, "E3.8.0.4", {"position": v(18.75, -2.79) * mm});
            skPoint(sketch, "E3.8.0.5", {"position": v(-6.25, -2.79) * mm});
            skLineSegment(sketch, "E3.8.0.6", {"start": v(-20, -3.29) * mm, "end": v(-15.83, -3.29) * mm, "construction": true});
            skLineSegment(sketch, "E3.8.0.7", {"start": v(9.17, -3.29) * mm, "end": v(11.67, -3.29) * mm});
            skPoint(sketch, "E3.8.0.8", {"position": v(6.25, -2.79) * mm});
            skPoint(sketch, "E3.8.0.9", {"position": v(-2.08, -2.79) * mm});
            skLineSegment(sketch, "E3.8.0.10", {"start": v(-7.5, -3.29) * mm, "end": v(-5, -3.29) * mm});
            skPoint(sketch, "E3.8.0.11", {"position": v(-18.75, -2.79) * mm});
            skLineSegment(sketch, "E3.8.0.12", {"start": v(-7.5, -2.29) * mm, "end": v(-5, -2.29) * mm});
            skLineSegment(sketch, "E3.8.0.13", {"start": v(-20, -2.29) * mm, "end": v(-17.5, -2.29) * mm});
            skLineSegment(sketch, "E3.8.0.14", {"start": v(-15.83, -3.29) * mm, "end": v(-13.33, -3.29) * mm});
            skLineSegment(sketch, "E3.8.0.15", {"start": v(-15.83, -2.29) * mm, "end": v(-13.33, -2.29) * mm});
            skLineSegment(sketch, "E3.8.0.16", {"start": v(-11.67, -3.29) * mm, "end": v(-9.17, -3.29) * mm});
            skLineSegment(sketch, "E3.8.0.17", {"start": v(-11.67, -2.29) * mm, "end": v(-9.17, -2.29) * mm});
            skLineSegment(sketch, "E3.8.0.18", {"start": v(9.17, -2.29) * mm, "end": v(11.67, -2.29) * mm});
            skLineSegment(sketch, "E3.8.0.19", {"start": v(17.5, -3.29) * mm, "end": v(20, -3.29) * mm});
            skLineSegment(sketch, "E3.8.0.20", {"start": v(0.83, -3.29) * mm, "end": v(3.33, -3.29) * mm});
            skLineSegment(sketch, "E3.8.0.21", {"start": v(13.33, -3.29) * mm, "end": v(15.83, -3.29) * mm});
            skLineSegment(sketch, "E3.8.0.22", {"start": v(-3.33, -3.29) * mm, "end": v(-0.83, -3.29) * mm});
            skPoint(sketch, "E3.8.0.23", {"position": v(10.42, -2.79) * mm});
            skPoint(sketch, "E3.8.0.24", {"position": v(-14.58, -2.79) * mm});
            skLineSegment(sketch, "E3.8.0.25", {"start": v(5, -3.29) * mm, "end": v(7.5, -3.29) * mm});
            skLineSegment(sketch, "E3.8.0.26", {"start": v(13.33, -2.29) * mm, "end": v(15.83, -2.29) * mm});
            skLineSegment(sketch, "E3.8.0.27", {"start": v(-3.33, -2.29) * mm, "end": v(-0.83, -2.29) * mm});
            skPoint(sketch, "E3.8.0.28", {"position": v(14.58, -2.79) * mm});
            skPoint(sketch, "E3.8.0.29", {"position": v(-10.42, -2.79) * mm});
            skLineSegment(sketch, "E3.8.0.30", {"start": v(-20, -3.29) * mm, "end": v(-17.5, -3.29) * mm});
            skLineSegment(sketch, "E3.8.0.31", {"start": v(20, -2.29) * mm, "end": v(20, -3.29) * mm});
            skLineSegment(sketch, "E3.8.0.32", {"start": v(9.17, -2.29) * mm, "end": v(9.17, -3.29) * mm});
            skLineSegment(sketch, "E3.8.0.33", {"start": v(3.33, -2.29) * mm, "end": v(3.33, -3.29) * mm});
            skLineSegment(sketch, "E3.8.0.34", {"start": v(15.83, -2.29) * mm, "end": v(15.83, -3.29) * mm});
            skLineSegment(sketch, "E3.8.0.35", {"start": v(-0.83, -2.29) * mm, "end": v(-0.83, -3.29) * mm});
            skLineSegment(sketch, "E3.8.0.36", {"start": v(11.67, -2.29) * mm, "end": v(11.67, -3.29) * mm});
            skLineSegment(sketch, "E3.8.0.37", {"start": v(7.5, -2.29) * mm, "end": v(7.5, -3.29) * mm});
            skLineSegment(sketch, "E3.8.0.38", {"start": v(17.5, -2.29) * mm, "end": v(17.5, -3.29) * mm});
            skLineSegment(sketch, "E3.8.0.39", {"start": v(0.83, -2.29) * mm, "end": v(0.83, -3.29) * mm});
            skLineSegment(sketch, "E3.8.0.40", {"start": v(13.33, -2.29) * mm, "end": v(13.33, -3.29) * mm});
            skLineSegment(sketch, "E3.8.0.41", {"start": v(-3.33, -2.29) * mm, "end": v(-3.33, -3.29) * mm});
            skLineSegment(sketch, "E3.8.0.42", {"start": v(-7.5, -2.29) * mm, "end": v(-7.5, -3.29) * mm});
            skLineSegment(sketch, "E3.8.0.43", {"start": v(-20, -2.29) * mm, "end": v(-20, -3.29) * mm});
            skLineSegment(sketch, "E3.8.0.44", {"start": v(-17.5, -2.29) * mm, "end": v(-17.5, -3.29) * mm});
            skLineSegment(sketch, "E3.8.0.45", {"start": v(-13.33, -2.29) * mm, "end": v(-13.33, -3.29) * mm});
            skLineSegment(sketch, "E3.8.0.46", {"start": v(-15.83, -2.29) * mm, "end": v(-15.83, -3.29) * mm});
            skLineSegment(sketch, "E3.8.0.47", {"start": v(-9.17, -2.29) * mm, "end": v(-9.17, -3.29) * mm});
            skLineSegment(sketch, "E3.8.0.48", {"start": v(-11.67, -2.29) * mm, "end": v(-11.67, -3.29) * mm});
            skLineSegment(sketch, "E3.8.0.49", {"start": v(5, -2.29) * mm, "end": v(5, -3.29) * mm});
            skLineSegment(sketch, "E3.8.0.50", {"start": v(-5, -2.29) * mm, "end": v(-5, -3.29) * mm});
            skPoint(sketch, "E3.9.0.0", {"position": v(2.08, -5.57) * mm});
            skLineSegment(sketch, "E3.9.0.1", {"start": v(5, -5.07) * mm, "end": v(7.5, -5.07) * mm});
            skLineSegment(sketch, "E3.9.0.2", {"start": v(17.5, -5.07) * mm, "end": v(20, -5.07) * mm});
            skLineSegment(sketch, "E3.9.0.3", {"start": v(0.83, -5.07) * mm, "end": v(3.33, -5.07) * mm});
            skPoint(sketch, "E3.9.0.4", {"position": v(18.75, -5.57) * mm});
            skPoint(sketch, "E3.9.0.5", {"position": v(-6.25, -5.57) * mm});
            skLineSegment(sketch, "E3.9.0.6", {"start": v(-20, -6.07) * mm, "end": v(-15.83, -6.07) * mm, "construction": true});
            skLineSegment(sketch, "E3.9.0.7", {"start": v(9.17, -6.07) * mm, "end": v(11.67, -6.07) * mm});
            skPoint(sketch, "E3.9.0.8", {"position": v(6.25, -5.57) * mm});
            skPoint(sketch, "E3.9.0.9", {"position": v(-2.08, -5.57) * mm});
            skLineSegment(sketch, "E3.9.0.10", {"start": v(-7.5, -6.07) * mm, "end": v(-5, -6.07) * mm});
            skPoint(sketch, "E3.9.0.11", {"position": v(-18.75, -5.57) * mm});
            skLineSegment(sketch, "E3.9.0.12", {"start": v(-7.5, -5.07) * mm, "end": v(-5, -5.07) * mm});
            skLineSegment(sketch, "E3.9.0.13", {"start": v(-20, -5.07) * mm, "end": v(-17.5, -5.07) * mm});
            skLineSegment(sketch, "E3.9.0.14", {"start": v(-15.83, -6.07) * mm, "end": v(-13.33, -6.07) * mm});
            skLineSegment(sketch, "E3.9.0.15", {"start": v(-15.83, -5.07) * mm, "end": v(-13.33, -5.07) * mm});
            skLineSegment(sketch, "E3.9.0.16", {"start": v(-11.67, -6.07) * mm, "end": v(-9.17, -6.07) * mm});
            skLineSegment(sketch, "E3.9.0.17", {"start": v(-11.67, -5.07) * mm, "end": v(-9.17, -5.07) * mm});
            skLineSegment(sketch, "E3.9.0.18", {"start": v(9.17, -5.07) * mm, "end": v(11.67, -5.07) * mm});
            skLineSegment(sketch, "E3.9.0.19", {"start": v(17.5, -6.07) * mm, "end": v(20, -6.07) * mm});
            skLineSegment(sketch, "E3.9.0.20", {"start": v(0.83, -6.07) * mm, "end": v(3.33, -6.07) * mm});
            skLineSegment(sketch, "E3.9.0.21", {"start": v(13.33, -6.07) * mm, "end": v(15.83, -6.07) * mm});
            skLineSegment(sketch, "E3.9.0.22", {"start": v(-3.33, -6.07) * mm, "end": v(-0.83, -6.07) * mm});
            skPoint(sketch, "E3.9.0.23", {"position": v(10.42, -5.57) * mm});
            skPoint(sketch, "E3.9.0.24", {"position": v(-14.58, -5.57) * mm});
            skLineSegment(sketch, "E3.9.0.25", {"start": v(5, -6.07) * mm, "end": v(7.5, -6.07) * mm});
            skLineSegment(sketch, "E3.9.0.26", {"start": v(13.33, -5.07) * mm, "end": v(15.83, -5.07) * mm});
            skLineSegment(sketch, "E3.9.0.27", {"start": v(-3.33, -5.07) * mm, "end": v(-0.83, -5.07) * mm});
            skPoint(sketch, "E3.9.0.28", {"position": v(14.58, -5.57) * mm});
            skPoint(sketch, "E3.9.0.29", {"position": v(-10.42, -5.57) * mm});
            skLineSegment(sketch, "E3.9.0.30", {"start": v(-20, -6.07) * mm, "end": v(-17.5, -6.07) * mm});
            skLineSegment(sketch, "E3.9.0.31", {"start": v(20, -5.07) * mm, "end": v(20, -6.07) * mm});
            skLineSegment(sketch, "E3.9.0.32", {"start": v(9.17, -5.07) * mm, "end": v(9.17, -6.07) * mm});
            skLineSegment(sketch, "E3.9.0.33", {"start": v(3.33, -5.07) * mm, "end": v(3.33, -6.07) * mm});
            skLineSegment(sketch, "E3.9.0.34", {"start": v(15.83, -5.07) * mm, "end": v(15.83, -6.07) * mm});
            skLineSegment(sketch, "E3.9.0.35", {"start": v(-0.83, -5.07) * mm, "end": v(-0.83, -6.07) * mm});
            skLineSegment(sketch, "E3.9.0.36", {"start": v(11.67, -5.07) * mm, "end": v(11.67, -6.07) * mm});
            skLineSegment(sketch, "E3.9.0.37", {"start": v(7.5, -5.07) * mm, "end": v(7.5, -6.07) * mm});
            skLineSegment(sketch, "E3.9.0.38", {"start": v(17.5, -5.07) * mm, "end": v(17.5, -6.07) * mm});
            skLineSegment(sketch, "E3.9.0.39", {"start": v(0.83, -5.07) * mm, "end": v(0.83, -6.07) * mm});
            skLineSegment(sketch, "E3.9.0.40", {"start": v(13.33, -5.07) * mm, "end": v(13.33, -6.07) * mm});
            skLineSegment(sketch, "E3.9.0.41", {"start": v(-3.33, -5.07) * mm, "end": v(-3.33, -6.07) * mm});
            skLineSegment(sketch, "E3.9.0.42", {"start": v(-7.5, -5.07) * mm, "end": v(-7.5, -6.07) * mm});
            skLineSegment(sketch, "E3.9.0.43", {"start": v(-20, -5.07) * mm, "end": v(-20, -6.07) * mm});
            skLineSegment(sketch, "E3.9.0.44", {"start": v(-17.5, -5.07) * mm, "end": v(-17.5, -6.07) * mm});
            skLineSegment(sketch, "E3.9.0.45", {"start": v(-13.33, -5.07) * mm, "end": v(-13.33, -6.07) * mm});
            skLineSegment(sketch, "E3.9.0.46", {"start": v(-15.83, -5.07) * mm, "end": v(-15.83, -6.07) * mm});
            skLineSegment(sketch, "E3.9.0.47", {"start": v(-9.17, -5.07) * mm, "end": v(-9.17, -6.07) * mm});
            skLineSegment(sketch, "E3.9.0.48", {"start": v(-11.67, -5.07) * mm, "end": v(-11.67, -6.07) * mm});
            skLineSegment(sketch, "E3.9.0.49", {"start": v(5, -5.07) * mm, "end": v(5, -6.07) * mm});
            skLineSegment(sketch, "E3.9.0.50", {"start": v(-5, -5.07) * mm, "end": v(-5, -6.07) * mm});
            skPoint(sketch, "E3.10.0.0", {"position": v(2.08, -8.36) * mm});
            skLineSegment(sketch, "E3.10.0.1", {"start": v(5, -7.86) * mm, "end": v(7.5, -7.86) * mm});
            skLineSegment(sketch, "E3.10.0.2", {"start": v(17.5, -7.86) * mm, "end": v(20, -7.86) * mm});
            skLineSegment(sketch, "E3.10.0.3", {"start": v(0.83, -7.86) * mm, "end": v(3.33, -7.86) * mm});
            skPoint(sketch, "E3.10.0.4", {"position": v(18.75, -8.36) * mm});
            skPoint(sketch, "E3.10.0.5", {"position": v(-6.25, -8.36) * mm});
            skLineSegment(sketch, "E3.10.0.6", {"start": v(-20, -8.86) * mm, "end": v(-15.83, -8.86) * mm, "construction": true});
            skLineSegment(sketch, "E3.10.0.7", {"start": v(9.17, -8.86) * mm, "end": v(11.67, -8.86) * mm});
            skPoint(sketch, "E3.10.0.8", {"position": v(6.25, -8.36) * mm});
            skPoint(sketch, "E3.10.0.9", {"position": v(-2.08, -8.36) * mm});
            skLineSegment(sketch, "E3.10.0.10", {"start": v(-7.5, -8.86) * mm, "end": v(-5, -8.86) * mm});
            skPoint(sketch, "E3.10.0.11", {"position": v(-18.75, -8.36) * mm});
            skLineSegment(sketch, "E3.10.0.12", {"start": v(-7.5, -7.86) * mm, "end": v(-5, -7.86) * mm});
            skLineSegment(sketch, "E3.10.0.13", {"start": v(-20, -7.86) * mm, "end": v(-17.5, -7.86) * mm});
            skLineSegment(sketch, "E3.10.0.14", {"start": v(-15.83, -8.86) * mm, "end": v(-13.33, -8.86) * mm});
            skLineSegment(sketch, "E3.10.0.15", {"start": v(-15.83, -7.86) * mm, "end": v(-13.33, -7.86) * mm});
            skLineSegment(sketch, "E3.10.0.16", {"start": v(-11.67, -8.86) * mm, "end": v(-9.17, -8.86) * mm});
            skLineSegment(sketch, "E3.10.0.17", {"start": v(-11.67, -7.86) * mm, "end": v(-9.17, -7.86) * mm});
            skLineSegment(sketch, "E3.10.0.18", {"start": v(9.17, -7.86) * mm, "end": v(11.67, -7.86) * mm});
            skLineSegment(sketch, "E3.10.0.19", {"start": v(17.5, -8.86) * mm, "end": v(20, -8.86) * mm});
            skLineSegment(sketch, "E3.10.0.20", {"start": v(0.83, -8.86) * mm, "end": v(3.33, -8.86) * mm});
            skLineSegment(sketch, "E3.10.0.21", {"start": v(13.33, -8.86) * mm, "end": v(15.83, -8.86) * mm});
            skLineSegment(sketch, "E3.10.0.22", {"start": v(-3.33, -8.86) * mm, "end": v(-0.83, -8.86) * mm});
            skPoint(sketch, "E3.10.0.23", {"position": v(10.42, -8.36) * mm});
            skPoint(sketch, "E3.10.0.24", {"position": v(-14.58, -8.36) * mm});
            skLineSegment(sketch, "E3.10.0.25", {"start": v(5, -8.86) * mm, "end": v(7.5, -8.86) * mm});
            skLineSegment(sketch, "E3.10.0.26", {"start": v(13.33, -7.86) * mm, "end": v(15.83, -7.86) * mm});
            skLineSegment(sketch, "E3.10.0.27", {"start": v(-3.33, -7.86) * mm, "end": v(-0.83, -7.86) * mm});
            skPoint(sketch, "E3.10.0.28", {"position": v(14.58, -8.36) * mm});
            skPoint(sketch, "E3.10.0.29", {"position": v(-10.42, -8.36) * mm});
            skLineSegment(sketch, "E3.10.0.30", {"start": v(-20, -8.86) * mm, "end": v(-17.5, -8.86) * mm});
            skLineSegment(sketch, "E3.10.0.31", {"start": v(20, -7.86) * mm, "end": v(20, -8.86) * mm});
            skLineSegment(sketch, "E3.10.0.32", {"start": v(9.17, -7.86) * mm, "end": v(9.17, -8.86) * mm});
            skLineSegment(sketch, "E3.10.0.33", {"start": v(3.33, -7.86) * mm, "end": v(3.33, -8.86) * mm});
            skLineSegment(sketch, "E3.10.0.34", {"start": v(15.83, -7.86) * mm, "end": v(15.83, -8.86) * mm});
            skLineSegment(sketch, "E3.10.0.35", {"start": v(-0.83, -7.86) * mm, "end": v(-0.83, -8.86) * mm});
            skLineSegment(sketch, "E3.10.0.36", {"start": v(11.67, -7.86) * mm, "end": v(11.67, -8.86) * mm});
            skLineSegment(sketch, "E3.10.0.37", {"start": v(7.5, -7.86) * mm, "end": v(7.5, -8.86) * mm});
            skLineSegment(sketch, "E3.10.0.38", {"start": v(17.5, -7.86) * mm, "end": v(17.5, -8.86) * mm});
            skLineSegment(sketch, "E3.10.0.39", {"start": v(0.83, -7.86) * mm, "end": v(0.83, -8.86) * mm});
            skLineSegment(sketch, "E3.10.0.40", {"start": v(13.33, -7.86) * mm, "end": v(13.33, -8.86) * mm});
            skLineSegment(sketch, "E3.10.0.41", {"start": v(-3.33, -7.86) * mm, "end": v(-3.33, -8.86) * mm});
            skLineSegment(sketch, "E3.10.0.42", {"start": v(-7.5, -7.86) * mm, "end": v(-7.5, -8.86) * mm});
            skLineSegment(sketch, "E3.10.0.43", {"start": v(-20, -7.86) * mm, "end": v(-20, -8.86) * mm});
            skLineSegment(sketch, "E3.10.0.44", {"start": v(-17.5, -7.86) * mm, "end": v(-17.5, -8.86) * mm});
            skLineSegment(sketch, "E3.10.0.45", {"start": v(-13.33, -7.86) * mm, "end": v(-13.33, -8.86) * mm});
            skLineSegment(sketch, "E3.10.0.46", {"start": v(-15.83, -7.86) * mm, "end": v(-15.83, -8.86) * mm});
            skLineSegment(sketch, "E3.10.0.47", {"start": v(-9.17, -7.86) * mm, "end": v(-9.17, -8.86) * mm});
            skLineSegment(sketch, "E3.10.0.48", {"start": v(-11.67, -7.86) * mm, "end": v(-11.67, -8.86) * mm});
            skLineSegment(sketch, "E3.10.0.49", {"start": v(5, -7.86) * mm, "end": v(5, -8.86) * mm});
            skLineSegment(sketch, "E3.10.0.50", {"start": v(-5, -7.86) * mm, "end": v(-5, -8.86) * mm});
            skPoint(sketch, "E3.11.0.0", {"position": v(2.08, -11.14) * mm});
            skLineSegment(sketch, "E3.11.0.1", {"start": v(5, -10.64) * mm, "end": v(7.5, -10.64) * mm});
            skLineSegment(sketch, "E3.11.0.2", {"start": v(17.5, -10.64) * mm, "end": v(20, -10.64) * mm});
            skLineSegment(sketch, "E3.11.0.3", {"start": v(0.83, -10.64) * mm, "end": v(3.33, -10.64) * mm});
            skPoint(sketch, "E3.11.0.4", {"position": v(18.75, -11.14) * mm});
            skPoint(sketch, "E3.11.0.5", {"position": v(-6.25, -11.14) * mm});
            skLineSegment(sketch, "E3.11.0.6", {"start": v(-20, -11.64) * mm, "end": v(-15.83, -11.64) * mm, "construction": true});
            skLineSegment(sketch, "E3.11.0.7", {"start": v(9.17, -11.64) * mm, "end": v(11.67, -11.64) * mm});
            skPoint(sketch, "E3.11.0.8", {"position": v(6.25, -11.14) * mm});
            skPoint(sketch, "E3.11.0.9", {"position": v(-2.08, -11.14) * mm});
            skLineSegment(sketch, "E3.11.0.10", {"start": v(-7.5, -11.64) * mm, "end": v(-5, -11.64) * mm});
            skPoint(sketch, "E3.11.0.11", {"position": v(-18.75, -11.14) * mm});
            skLineSegment(sketch, "E3.11.0.12", {"start": v(-7.5, -10.64) * mm, "end": v(-5, -10.64) * mm});
            skLineSegment(sketch, "E3.11.0.13", {"start": v(-20, -10.64) * mm, "end": v(-17.5, -10.64) * mm});
            skLineSegment(sketch, "E3.11.0.14", {"start": v(-15.83, -11.64) * mm, "end": v(-13.33, -11.64) * mm});
            skLineSegment(sketch, "E3.11.0.15", {"start": v(-15.83, -10.64) * mm, "end": v(-13.33, -10.64) * mm});
            skLineSegment(sketch, "E3.11.0.16", {"start": v(-11.67, -11.64) * mm, "end": v(-9.17, -11.64) * mm});
            skLineSegment(sketch, "E3.11.0.17", {"start": v(-11.67, -10.64) * mm, "end": v(-9.17, -10.64) * mm});
            skLineSegment(sketch, "E3.11.0.18", {"start": v(9.17, -10.64) * mm, "end": v(11.67, -10.64) * mm});
            skLineSegment(sketch, "E3.11.0.19", {"start": v(17.5, -11.64) * mm, "end": v(20, -11.64) * mm});
            skLineSegment(sketch, "E3.11.0.20", {"start": v(0.83, -11.64) * mm, "end": v(3.33, -11.64) * mm});
            skLineSegment(sketch, "E3.11.0.21", {"start": v(13.33, -11.64) * mm, "end": v(15.83, -11.64) * mm});
            skLineSegment(sketch, "E3.11.0.22", {"start": v(-3.33, -11.64) * mm, "end": v(-0.83, -11.64) * mm});
            skPoint(sketch, "E3.11.0.23", {"position": v(10.42, -11.14) * mm});
            skPoint(sketch, "E3.11.0.24", {"position": v(-14.58, -11.14) * mm});
            skLineSegment(sketch, "E3.11.0.25", {"start": v(5, -11.64) * mm, "end": v(7.5, -11.64) * mm});
            skLineSegment(sketch, "E3.11.0.26", {"start": v(13.33, -10.64) * mm, "end": v(15.83, -10.64) * mm});
            skLineSegment(sketch, "E3.11.0.27", {"start": v(-3.33, -10.64) * mm, "end": v(-0.83, -10.64) * mm});
            skPoint(sketch, "E3.11.0.28", {"position": v(14.58, -11.14) * mm});
            skPoint(sketch, "E3.11.0.29", {"position": v(-10.42, -11.14) * mm});
            skLineSegment(sketch, "E3.11.0.30", {"start": v(-20, -11.64) * mm, "end": v(-17.5, -11.64) * mm});
            skLineSegment(sketch, "E3.11.0.31", {"start": v(20, -10.64) * mm, "end": v(20, -11.64) * mm});
            skLineSegment(sketch, "E3.11.0.32", {"start": v(9.17, -10.64) * mm, "end": v(9.17, -11.64) * mm});
            skLineSegment(sketch, "E3.11.0.33", {"start": v(3.33, -10.64) * mm, "end": v(3.33, -11.64) * mm});
            skLineSegment(sketch, "E3.11.0.34", {"start": v(15.83, -10.64) * mm, "end": v(15.83, -11.64) * mm});
            skLineSegment(sketch, "E3.11.0.35", {"start": v(-0.83, -10.64) * mm, "end": v(-0.83, -11.64) * mm});
            skLineSegment(sketch, "E3.11.0.36", {"start": v(11.67, -10.64) * mm, "end": v(11.67, -11.64) * mm});
            skLineSegment(sketch, "E3.11.0.37", {"start": v(7.5, -10.64) * mm, "end": v(7.5, -11.64) * mm});
            skLineSegment(sketch, "E3.11.0.38", {"start": v(17.5, -10.64) * mm, "end": v(17.5, -11.64) * mm});
            skLineSegment(sketch, "E3.11.0.39", {"start": v(0.83, -10.64) * mm, "end": v(0.83, -11.64) * mm});
            skLineSegment(sketch, "E3.11.0.40", {"start": v(13.33, -10.64) * mm, "end": v(13.33, -11.64) * mm});
            skLineSegment(sketch, "E3.11.0.41", {"start": v(-3.33, -10.64) * mm, "end": v(-3.33, -11.64) * mm});
            skLineSegment(sketch, "E3.11.0.42", {"start": v(-7.5, -10.64) * mm, "end": v(-7.5, -11.64) * mm});
            skLineSegment(sketch, "E3.11.0.43", {"start": v(-20, -10.64) * mm, "end": v(-20, -11.64) * mm});
            skLineSegment(sketch, "E3.11.0.44", {"start": v(-17.5, -10.64) * mm, "end": v(-17.5, -11.64) * mm});
            skLineSegment(sketch, "E3.11.0.45", {"start": v(-13.33, -10.64) * mm, "end": v(-13.33, -11.64) * mm});
            skLineSegment(sketch, "E3.11.0.46", {"start": v(-15.83, -10.64) * mm, "end": v(-15.83, -11.64) * mm});
            skLineSegment(sketch, "E3.11.0.47", {"start": v(-9.17, -10.64) * mm, "end": v(-9.17, -11.64) * mm});
            skLineSegment(sketch, "E3.11.0.48", {"start": v(-11.67, -10.64) * mm, "end": v(-11.67, -11.64) * mm});
            skLineSegment(sketch, "E3.11.0.49", {"start": v(5, -10.64) * mm, "end": v(5, -11.64) * mm});
            skLineSegment(sketch, "E3.11.0.50", {"start": v(-5, -10.64) * mm, "end": v(-5, -11.64) * mm});
            skPoint(sketch, "E3.12.0.0", {"position": v(2.08, -13.93) * mm});
            skLineSegment(sketch, "E3.12.0.1", {"start": v(5, -13.43) * mm, "end": v(7.5, -13.43) * mm});
            skLineSegment(sketch, "E3.12.0.2", {"start": v(17.5, -13.43) * mm, "end": v(20, -13.43) * mm});
            skLineSegment(sketch, "E3.12.0.3", {"start": v(0.83, -13.43) * mm, "end": v(3.33, -13.43) * mm});
            skPoint(sketch, "E3.12.0.4", {"position": v(18.75, -13.93) * mm});
            skPoint(sketch, "E3.12.0.5", {"position": v(-6.25, -13.93) * mm});
            skLineSegment(sketch, "E3.12.0.6", {"start": v(-20, -14.43) * mm, "end": v(-15.83, -14.43) * mm, "construction": true});
            skLineSegment(sketch, "E3.12.0.7", {"start": v(9.17, -14.43) * mm, "end": v(11.67, -14.43) * mm});
            skPoint(sketch, "E3.12.0.8", {"position": v(6.25, -13.93) * mm});
            skPoint(sketch, "E3.12.0.9", {"position": v(-2.08, -13.93) * mm});
            skLineSegment(sketch, "E3.12.0.10", {"start": v(-7.5, -14.43) * mm, "end": v(-5, -14.43) * mm});
            skPoint(sketch, "E3.12.0.11", {"position": v(-18.75, -13.93) * mm});
            skLineSegment(sketch, "E3.12.0.12", {"start": v(-7.5, -13.43) * mm, "end": v(-5, -13.43) * mm});
            skLineSegment(sketch, "E3.12.0.13", {"start": v(-20, -13.43) * mm, "end": v(-17.5, -13.43) * mm});
            skLineSegment(sketch, "E3.12.0.14", {"start": v(-15.83, -14.43) * mm, "end": v(-13.33, -14.43) * mm});
            skLineSegment(sketch, "E3.12.0.15", {"start": v(-15.83, -13.43) * mm, "end": v(-13.33, -13.43) * mm});
            skLineSegment(sketch, "E3.12.0.16", {"start": v(-11.67, -14.43) * mm, "end": v(-9.17, -14.43) * mm});
            skLineSegment(sketch, "E3.12.0.17", {"start": v(-11.67, -13.43) * mm, "end": v(-9.17, -13.43) * mm});
            skLineSegment(sketch, "E3.12.0.18", {"start": v(9.17, -13.43) * mm, "end": v(11.67, -13.43) * mm});
            skLineSegment(sketch, "E3.12.0.19", {"start": v(17.5, -14.43) * mm, "end": v(20, -14.43) * mm});
            skLineSegment(sketch, "E3.12.0.20", {"start": v(0.83, -14.43) * mm, "end": v(3.33, -14.43) * mm});
            skLineSegment(sketch, "E3.12.0.21", {"start": v(13.33, -14.43) * mm, "end": v(15.83, -14.43) * mm});
            skLineSegment(sketch, "E3.12.0.22", {"start": v(-3.33, -14.43) * mm, "end": v(-0.83, -14.43) * mm});
            skPoint(sketch, "E3.12.0.23", {"position": v(10.42, -13.93) * mm});
            skPoint(sketch, "E3.12.0.24", {"position": v(-14.58, -13.93) * mm});
            skLineSegment(sketch, "E3.12.0.25", {"start": v(5, -14.43) * mm, "end": v(7.5, -14.43) * mm});
            skLineSegment(sketch, "E3.12.0.26", {"start": v(13.33, -13.43) * mm, "end": v(15.83, -13.43) * mm});
            skLineSegment(sketch, "E3.12.0.27", {"start": v(-3.33, -13.43) * mm, "end": v(-0.83, -13.43) * mm});
            skPoint(sketch, "E3.12.0.28", {"position": v(14.58, -13.93) * mm});
            skPoint(sketch, "E3.12.0.29", {"position": v(-10.42, -13.93) * mm});
            skLineSegment(sketch, "E3.12.0.30", {"start": v(-20, -14.43) * mm, "end": v(-17.5, -14.43) * mm});
            skLineSegment(sketch, "E3.12.0.31", {"start": v(20, -13.43) * mm, "end": v(20, -14.43) * mm});
            skLineSegment(sketch, "E3.12.0.32", {"start": v(9.17, -13.43) * mm, "end": v(9.17, -14.43) * mm});
            skLineSegment(sketch, "E3.12.0.33", {"start": v(3.33, -13.43) * mm, "end": v(3.33, -14.43) * mm});
            skLineSegment(sketch, "E3.12.0.34", {"start": v(15.83, -13.43) * mm, "end": v(15.83, -14.43) * mm});
            skLineSegment(sketch, "E3.12.0.35", {"start": v(-0.83, -13.43) * mm, "end": v(-0.83, -14.43) * mm});
            skLineSegment(sketch, "E3.12.0.36", {"start": v(11.67, -13.43) * mm, "end": v(11.67, -14.43) * mm});
            skLineSegment(sketch, "E3.12.0.37", {"start": v(7.5, -13.43) * mm, "end": v(7.5, -14.43) * mm});
            skLineSegment(sketch, "E3.12.0.38", {"start": v(17.5, -13.43) * mm, "end": v(17.5, -14.43) * mm});
            skLineSegment(sketch, "E3.12.0.39", {"start": v(0.83, -13.43) * mm, "end": v(0.83, -14.43) * mm});
            skLineSegment(sketch, "E3.12.0.40", {"start": v(13.33, -13.43) * mm, "end": v(13.33, -14.43) * mm});
            skLineSegment(sketch, "E3.12.0.41", {"start": v(-3.33, -13.43) * mm, "end": v(-3.33, -14.43) * mm});
            skLineSegment(sketch, "E3.12.0.42", {"start": v(-7.5, -13.43) * mm, "end": v(-7.5, -14.43) * mm});
            skLineSegment(sketch, "E3.12.0.43", {"start": v(-20, -13.43) * mm, "end": v(-20, -14.43) * mm});
            skLineSegment(sketch, "E3.12.0.44", {"start": v(-17.5, -13.43) * mm, "end": v(-17.5, -14.43) * mm});
            skLineSegment(sketch, "E3.12.0.45", {"start": v(-13.33, -13.43) * mm, "end": v(-13.33, -14.43) * mm});
            skLineSegment(sketch, "E3.12.0.46", {"start": v(-15.83, -13.43) * mm, "end": v(-15.83, -14.43) * mm});
            skLineSegment(sketch, "E3.12.0.47", {"start": v(-9.17, -13.43) * mm, "end": v(-9.17, -14.43) * mm});
            skLineSegment(sketch, "E3.12.0.48", {"start": v(-11.67, -13.43) * mm, "end": v(-11.67, -14.43) * mm});
            skLineSegment(sketch, "E3.12.0.49", {"start": v(5, -13.43) * mm, "end": v(5, -14.43) * mm});
            skLineSegment(sketch, "E3.12.0.50", {"start": v(-5, -13.43) * mm, "end": v(-5, -14.43) * mm});
            skPoint(sketch, "E3.13.0.0", {"position": v(2.08, -16.71) * mm});
            skLineSegment(sketch, "E3.13.0.1", {"start": v(5, -16.21) * mm, "end": v(7.5, -16.21) * mm});
            skLineSegment(sketch, "E3.13.0.2", {"start": v(17.5, -16.21) * mm, "end": v(20, -16.21) * mm});
            skLineSegment(sketch, "E3.13.0.3", {"start": v(0.83, -16.21) * mm, "end": v(3.33, -16.21) * mm});
            skPoint(sketch, "E3.13.0.4", {"position": v(18.75, -16.71) * mm});
            skPoint(sketch, "E3.13.0.5", {"position": v(-6.25, -16.71) * mm});
            skLineSegment(sketch, "E3.13.0.6", {"start": v(-20, -17.21) * mm, "end": v(-15.83, -17.21) * mm, "construction": true});
            skLineSegment(sketch, "E3.13.0.7", {"start": v(9.17, -17.21) * mm, "end": v(11.67, -17.21) * mm});
            skPoint(sketch, "E3.13.0.8", {"position": v(6.25, -16.71) * mm});
            skPoint(sketch, "E3.13.0.9", {"position": v(-2.08, -16.71) * mm});
            skLineSegment(sketch, "E3.13.0.10", {"start": v(-7.5, -17.21) * mm, "end": v(-5, -17.21) * mm});
            skPoint(sketch, "E3.13.0.11", {"position": v(-18.75, -16.71) * mm});
            skLineSegment(sketch, "E3.13.0.12", {"start": v(-7.5, -16.21) * mm, "end": v(-5, -16.21) * mm});
            skLineSegment(sketch, "E3.13.0.13", {"start": v(-20, -16.21) * mm, "end": v(-17.5, -16.21) * mm});
            skLineSegment(sketch, "E3.13.0.14", {"start": v(-15.83, -17.21) * mm, "end": v(-13.33, -17.21) * mm});
            skLineSegment(sketch, "E3.13.0.15", {"start": v(-15.83, -16.21) * mm, "end": v(-13.33, -16.21) * mm});
            skLineSegment(sketch, "E3.13.0.16", {"start": v(-11.67, -17.21) * mm, "end": v(-9.17, -17.21) * mm});
            skLineSegment(sketch, "E3.13.0.17", {"start": v(-11.67, -16.21) * mm, "end": v(-9.17, -16.21) * mm});
            skLineSegment(sketch, "E3.13.0.18", {"start": v(9.17, -16.21) * mm, "end": v(11.67, -16.21) * mm});
            skLineSegment(sketch, "E3.13.0.19", {"start": v(17.5, -17.21) * mm, "end": v(20, -17.21) * mm});
            skLineSegment(sketch, "E3.13.0.20", {"start": v(0.83, -17.21) * mm, "end": v(3.33, -17.21) * mm});
            skLineSegment(sketch, "E3.13.0.21", {"start": v(13.33, -17.21) * mm, "end": v(15.83, -17.21) * mm});
            skLineSegment(sketch, "E3.13.0.22", {"start": v(-3.33, -17.21) * mm, "end": v(-0.83, -17.21) * mm});
            skPoint(sketch, "E3.13.0.23", {"position": v(10.42, -16.71) * mm});
            skPoint(sketch, "E3.13.0.24", {"position": v(-14.58, -16.71) * mm});
            skLineSegment(sketch, "E3.13.0.25", {"start": v(5, -17.21) * mm, "end": v(7.5, -17.21) * mm});
            skLineSegment(sketch, "E3.13.0.26", {"start": v(13.33, -16.21) * mm, "end": v(15.83, -16.21) * mm});
            skLineSegment(sketch, "E3.13.0.27", {"start": v(-3.33, -16.21) * mm, "end": v(-0.83, -16.21) * mm});
            skPoint(sketch, "E3.13.0.28", {"position": v(14.58, -16.71) * mm});
            skPoint(sketch, "E3.13.0.29", {"position": v(-10.42, -16.71) * mm});
            skLineSegment(sketch, "E3.13.0.30", {"start": v(-20, -17.21) * mm, "end": v(-17.5, -17.21) * mm});
            skLineSegment(sketch, "E3.13.0.31", {"start": v(20, -16.21) * mm, "end": v(20, -17.21) * mm});
            skLineSegment(sketch, "E3.13.0.32", {"start": v(9.17, -16.21) * mm, "end": v(9.17, -17.21) * mm});
            skLineSegment(sketch, "E3.13.0.33", {"start": v(3.33, -16.21) * mm, "end": v(3.33, -17.21) * mm});
            skLineSegment(sketch, "E3.13.0.34", {"start": v(15.83, -16.21) * mm, "end": v(15.83, -17.21) * mm});
            skLineSegment(sketch, "E3.13.0.35", {"start": v(-0.83, -16.21) * mm, "end": v(-0.83, -17.21) * mm});
            skLineSegment(sketch, "E3.13.0.36", {"start": v(11.67, -16.21) * mm, "end": v(11.67, -17.21) * mm});
            skLineSegment(sketch, "E3.13.0.37", {"start": v(7.5, -16.21) * mm, "end": v(7.5, -17.21) * mm});
            skLineSegment(sketch, "E3.13.0.38", {"start": v(17.5, -16.21) * mm, "end": v(17.5, -17.21) * mm});
            skLineSegment(sketch, "E3.13.0.39", {"start": v(0.83, -16.21) * mm, "end": v(0.83, -17.21) * mm});
            skLineSegment(sketch, "E3.13.0.40", {"start": v(13.33, -16.21) * mm, "end": v(13.33, -17.21) * mm});
            skLineSegment(sketch, "E3.13.0.41", {"start": v(-3.33, -16.21) * mm, "end": v(-3.33, -17.21) * mm});
            skLineSegment(sketch, "E3.13.0.42", {"start": v(-7.5, -16.21) * mm, "end": v(-7.5, -17.21) * mm});
            skLineSegment(sketch, "E3.13.0.43", {"start": v(-20, -16.21) * mm, "end": v(-20, -17.21) * mm});
            skLineSegment(sketch, "E3.13.0.44", {"start": v(-17.5, -16.21) * mm, "end": v(-17.5, -17.21) * mm});
            skLineSegment(sketch, "E3.13.0.45", {"start": v(-13.33, -16.21) * mm, "end": v(-13.33, -17.21) * mm});
            skLineSegment(sketch, "E3.13.0.46", {"start": v(-15.83, -16.21) * mm, "end": v(-15.83, -17.21) * mm});
            skLineSegment(sketch, "E3.13.0.47", {"start": v(-9.17, -16.21) * mm, "end": v(-9.17, -17.21) * mm});
            skLineSegment(sketch, "E3.13.0.48", {"start": v(-11.67, -16.21) * mm, "end": v(-11.67, -17.21) * mm});
            skLineSegment(sketch, "E3.13.0.49", {"start": v(5, -16.21) * mm, "end": v(5, -17.21) * mm});
            skLineSegment(sketch, "E3.13.0.50", {"start": v(-5, -16.21) * mm, "end": v(-5, -17.21) * mm});
            skLineSegment(sketch, "E3.direction1", {"start": v(-20, 19) * mm, "end": v(-20, 16.21) * mm, "construction": true});
            skPoint(sketch, "E4.0.14.0", {"position": v(2.08, -19.5) * mm});
            skLineSegment(sketch, "E4.1.14.0", {"start": v(5, -19) * mm, "end": v(7.5, -19) * mm});
            skLineSegment(sketch, "E4.4.14.0", {"start": v(17.5, -19) * mm, "end": v(20, -19) * mm});
            skLineSegment(sketch, "E4.7.14.0", {"start": v(0.83, -19) * mm, "end": v(3.33, -19) * mm});
            skPoint(sketch, "E4.10.14.0", {"position": v(18.75, -19.5) * mm});
            skPoint(sketch, "E4.11.14.0", {"position": v(-6.25, -19.5) * mm});
            skLineSegment(sketch, "E4.12.14.0", {"start": v(-20, -20) * mm, "end": v(-15.83, -20) * mm, "construction": true});
            skLineSegment(sketch, "E4.15.14.0", {"start": v(9.17, -20) * mm, "end": v(11.67, -20) * mm});
            skPoint(sketch, "E4.18.14.0", {"position": v(6.25, -19.5) * mm});
            skPoint(sketch, "E4.19.14.0", {"position": v(-2.08, -19.5) * mm});
            skLineSegment(sketch, "E4.20.14.0", {"start": v(-7.5, -20) * mm, "end": v(-5, -20) * mm});
            skPoint(sketch, "E4.23.14.0", {"position": v(-18.75, -19.5) * mm});
            skLineSegment(sketch, "E4.24.14.0", {"start": v(-7.5, -19) * mm, "end": v(-5, -19) * mm});
            skLineSegment(sketch, "E4.27.14.0", {"start": v(-20, -19) * mm, "end": v(-17.5, -19) * mm});
            skLineSegment(sketch, "E4.30.14.0", {"start": v(-15.83, -20) * mm, "end": v(-13.33, -20) * mm});
            skLineSegment(sketch, "E4.33.14.0", {"start": v(-15.83, -19) * mm, "end": v(-13.33, -19) * mm});
            skLineSegment(sketch, "E4.36.14.0", {"start": v(-11.67, -20) * mm, "end": v(-9.17, -20) * mm});
            skLineSegment(sketch, "E4.39.14.0", {"start": v(-11.67, -19) * mm, "end": v(-9.17, -19) * mm});
            skLineSegment(sketch, "E4.42.14.0", {"start": v(9.17, -19) * mm, "end": v(11.67, -19) * mm});
            skLineSegment(sketch, "E4.45.14.0", {"start": v(17.5, -20) * mm, "end": v(20, -20) * mm});
            skLineSegment(sketch, "E4.48.14.0", {"start": v(0.83, -20) * mm, "end": v(3.33, -20) * mm});
            skLineSegment(sketch, "E4.51.14.0", {"start": v(13.33, -20) * mm, "end": v(15.83, -20) * mm});
            skLineSegment(sketch, "E4.54.14.0", {"start": v(-3.33, -20) * mm, "end": v(-0.83, -20) * mm});
            skPoint(sketch, "E4.57.14.0", {"position": v(10.42, -19.5) * mm});
            skPoint(sketch, "E4.58.14.0", {"position": v(-14.58, -19.5) * mm});
            skLineSegment(sketch, "E4.59.14.0", {"start": v(5, -20) * mm, "end": v(7.5, -20) * mm});
            skLineSegment(sketch, "E4.62.14.0", {"start": v(13.33, -19) * mm, "end": v(15.83, -19) * mm});
            skLineSegment(sketch, "E4.65.14.0", {"start": v(-3.33, -19) * mm, "end": v(-0.83, -19) * mm});
            skPoint(sketch, "E4.68.14.0", {"position": v(14.58, -19.5) * mm});
            skPoint(sketch, "E4.69.14.0", {"position": v(-10.42, -19.5) * mm});
            skLineSegment(sketch, "E4.70.14.0", {"start": v(-20, -20) * mm, "end": v(-17.5, -20) * mm});
            skLineSegment(sketch, "E4.73.14.0", {"start": v(20, -19) * mm, "end": v(20, -20) * mm});
            skLineSegment(sketch, "E4.76.14.0", {"start": v(9.17, -19) * mm, "end": v(9.17, -20) * mm});
            skLineSegment(sketch, "E4.79.14.0", {"start": v(3.33, -19) * mm, "end": v(3.33, -20) * mm});
            skLineSegment(sketch, "E4.82.14.0", {"start": v(15.83, -19) * mm, "end": v(15.83, -20) * mm});
            skLineSegment(sketch, "E4.85.14.0", {"start": v(-0.83, -19) * mm, "end": v(-0.83, -20) * mm});
            skLineSegment(sketch, "E4.88.14.0", {"start": v(11.67, -19) * mm, "end": v(11.67, -20) * mm});
            skLineSegment(sketch, "E4.91.14.0", {"start": v(7.5, -19) * mm, "end": v(7.5, -20) * mm});
            skLineSegment(sketch, "E4.94.14.0", {"start": v(17.5, -19) * mm, "end": v(17.5, -20) * mm});
            skLineSegment(sketch, "E4.97.14.0", {"start": v(0.83, -19) * mm, "end": v(0.83, -20) * mm});
            skLineSegment(sketch, "E4.100.14.0", {"start": v(13.33, -19) * mm, "end": v(13.33, -20) * mm});
            skLineSegment(sketch, "E4.103.14.0", {"start": v(-3.33, -19) * mm, "end": v(-3.33, -20) * mm});
            skLineSegment(sketch, "E4.106.14.0", {"start": v(-7.5, -19) * mm, "end": v(-7.5, -20) * mm});
            skLineSegment(sketch, "E4.109.14.0", {"start": v(-20, -19) * mm, "end": v(-20, -20) * mm});
            skLineSegment(sketch, "E4.112.14.0", {"start": v(-17.5, -19) * mm, "end": v(-17.5, -20) * mm});
            skLineSegment(sketch, "E4.115.14.0", {"start": v(-13.33, -19) * mm, "end": v(-13.33, -20) * mm});
            skLineSegment(sketch, "E4.118.14.0", {"start": v(-15.83, -19) * mm, "end": v(-15.83, -20) * mm});
            skLineSegment(sketch, "E4.121.14.0", {"start": v(-9.17, -19) * mm, "end": v(-9.17, -20) * mm});
            skLineSegment(sketch, "E4.124.14.0", {"start": v(-11.67, -19) * mm, "end": v(-11.67, -20) * mm});
            skLineSegment(sketch, "E4.127.14.0", {"start": v(5, -19) * mm, "end": v(5, -20) * mm});
            skLineSegment(sketch, "E4.130.14.0", {"start": v(-5, -19) * mm, "end": v(-5, -20) * mm});
            skSolve(sketch);
        }
        {
            var Q0;
            Q0 = qSketchRegion(id + "F2", true);
            extrude(context, id + "F3", {"entities" : qUnion([Q0]), "operationType" : NewBodyOperationType.ADD, "depth" : 8.2 * mm, "offsetDistance" : 25 * mm});
        }
    });
